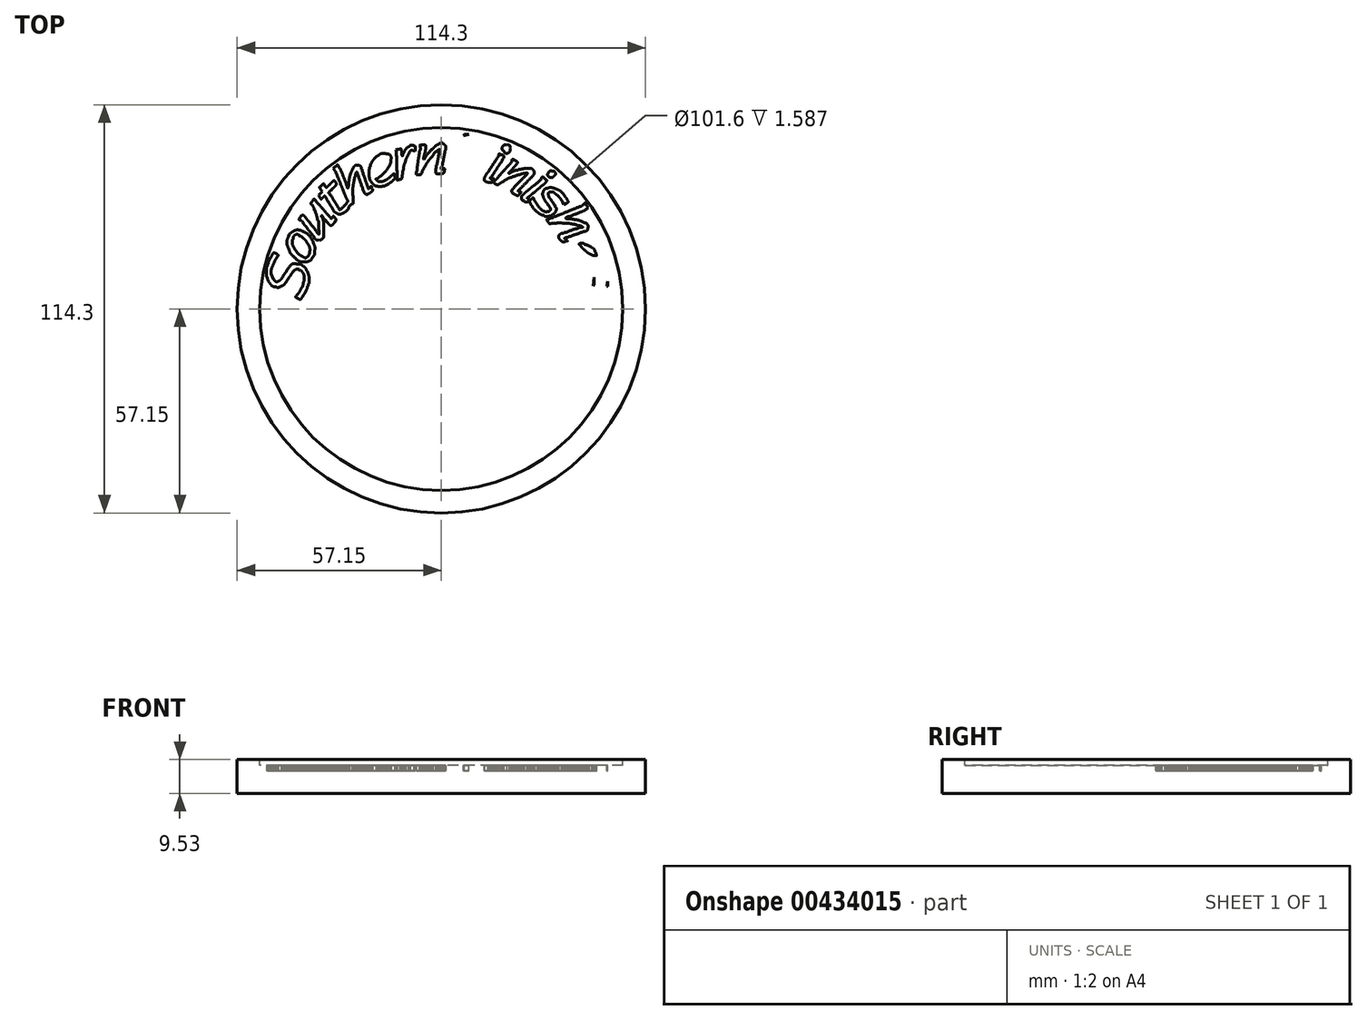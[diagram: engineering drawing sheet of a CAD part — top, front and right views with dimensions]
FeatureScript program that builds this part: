
annotation { "Feature Type Name" : "Feature", "Feature Type Description" : "" }
export const myFeature = defineFeature(function(context is Context, id is Id, definition is map)
    precondition{}
    {
        {
            var Q0;
            Q0=qCreatedBy(makeId("Top.planeOp"),FACE);
            var sketch = newSketch(context, id + "F0", { "sketchPlane" : qUnion([Q0])});
            skCircle(sketch, "E0", {"center": v(0, 0) * mm, "radius": 57.15 * mm});
            skSolve(sketch);
        }
        {
            var Q0;
            Q0 = qSketchRegion(id + "F0", true);
            extrude(context, id + "F1", {"entities" : qUnion([Q0]), "oppositeDirection" : true, "depth" : 9.52 * mm});
        }
        {
            var Q0;
            Q0=qCreatedBy(makeId("Top.planeOp"),FACE);
            var sketch = newSketch(context, id + "F2", { "sketchPlane" : qUnion([Q0])});
            skCircle(sketch, "E1", {"center": v(0, 0) * mm, "radius": 50.8 * mm});
            skSolve(sketch);
        }
        {
            var Q0;
            Q0 = qSketchRegion(id + "F2", true);
            var Q1;
            Q1 = qConstructionFilter(qBodyType(qCreatedBy(id + "F2" ,EDGE), BodyType.WIRE), ConstructionObject.NO);
            extrude(context, id + "F3", {"entities" : qUnion([Q0]), "operationType" : NewBodyOperationType.REMOVE, "surfaceEntities" : qUnion([Q1]), "oppositeDirection" : true, "depth" : 1.59 * mm});
        }
        {
            var Q0;
            Q0=makeQuery(id+"F3.boolean.opBoolean","COPY",FACE,{"derivedFrom":makeQuery(id+"F3.opExtrude","CAP_FACE",FACE,{"disambiguationData":[OSD([sQuery(id+"F2.wireOp",EDGE,"E1")])],"isStart":false})});
            var sketch = newSketch(context, id + "F4", { "sketchPlane" : qUnion([Q0])});
            skFitSpline(sketch, "E2", {"points": [v(-39.96, 2.84) * mm, v(-40.13, 2.95) * mm, v(-40.38, 3.08) * mm, v(-40.51, 3.14) * mm]});
            skFitSpline(sketch, "E3", {"points": [v(-40.51, 3.14) * mm, v(-40.64, 3.2) * mm, v(-40.75, 3.27) * mm, v(-40.75, 3.3) * mm]});
            skFitSpline(sketch, "E4", {"points": [v(-40.75, 3.3) * mm, v(-40.75, 3.4) * mm, v(-40.5, 3.8) * mm, v(-40.3, 4.03) * mm]});
            skFitSpline(sketch, "E5", {"points": [v(-40.3, 4.03) * mm, v(-39.88, 4.52) * mm, v(-39.62, 4.9) * mm, v(-39.38, 5.4) * mm]});
            skFitSpline(sketch, "E6", {"points": [v(-39.38, 5.4) * mm, v(-39.24, 5.7) * mm, v(-39.1, 5.95) * mm, v(-39.06, 5.98) * mm]});
            skFitSpline(sketch, "E7", {"points": [v(-39.06, 5.98) * mm, v(-38.95, 6.08) * mm, v(-38.65, 6.98) * mm, v(-38.65, 7.2) * mm]});
            skFitSpline(sketch, "E8", {"points": [v(-38.65, 7.2) * mm, v(-38.65, 7.33) * mm, v(-38.6, 7.46) * mm, v(-38.56, 7.5) * mm]});
            skFitSpline(sketch, "E9", {"points": [v(-38.56, 7.5) * mm, v(-38.5, 7.52) * mm, v(-38.44, 7.93) * mm, v(-38.4, 8.4) * mm]});
            skFitSpline(sketch, "E10", {"points": [v(-38.4, 8.4) * mm, v(-38.34, 9.07) * mm, v(-38.36, 9.32) * mm, v(-38.5, 9.63) * mm]});
            skFitSpline(sketch, "E11", {"points": [v(-38.5, 9.63) * mm, v(-38.69, 10.05) * mm, v(-39.44, 10.8) * mm, v(-39.67, 10.8) * mm]});
            skFitSpline(sketch, "E12", {"points": [v(-39.67, 10.8) * mm, v(-39.74, 10.8) * mm, v(-39.8, 10.85) * mm, v(-39.8, 10.9) * mm]});
            skFitSpline(sketch, "E13", {"points": [v(-39.8, 10.9) * mm, v(-39.8, 11.08) * mm, v(-40.56, 11.12) * mm, v(-40.89, 10.95) * mm]});
            skFitSpline(sketch, "E14", {"points": [v(-40.89, 10.95) * mm, v(-41.25, 10.76) * mm, v(-41.48, 10.55) * mm, v(-41.48, 10.41) * mm]});
            skFitSpline(sketch, "E15", {"points": [v(-41.48, 10.41) * mm, v(-41.48, 10.36) * mm, v(-41.58, 10.23) * mm, v(-41.7, 10.12) * mm]});
            skFitSpline(sketch, "E16", {"points": [v(-41.7, 10.12) * mm, v(-41.82, 10.01) * mm, v(-41.98, 9.78) * mm, v(-42.07, 9.6) * mm]});
            skFitSpline(sketch, "E17", {"points": [v(-42.07, 9.6) * mm, v(-42.16, 9.41) * mm, v(-42.3, 9.17) * mm, v(-42.4, 9.06) * mm]});
            skFitSpline(sketch, "E18", {"points": [v(-42.4, 9.06) * mm, v(-42.5, 8.95) * mm, v(-42.85, 8.46) * mm, v(-43.18, 7.97) * mm]});
            skFitSpline(sketch, "E19", {"points": [v(-43.18, 7.97) * mm, v(-43.84, 7) * mm, v(-44.17, 6.65) * mm, v(-44.74, 6.38) * mm]});
            skFitSpline(sketch, "E20", {"points": [v(-44.74, 6.38) * mm, v(-45.43, 6.06) * mm, v(-45.87, 5.96) * mm, v(-46.1, 6.08) * mm]});
            skFitSpline(sketch, "E21", {"points": [v(-46.1, 6.08) * mm, v(-46.2, 6.14) * mm, v(-46.4, 6.19) * mm, v(-46.51, 6.19) * mm]});
            skFitSpline(sketch, "E22", {"points": [v(-46.51, 6.19) * mm, v(-46.85, 6.19) * mm, v(-47.56, 6.6) * mm, v(-47.83, 6.96) * mm]});
            skFitSpline(sketch, "E23", {"points": [v(-47.83, 6.96) * mm, v(-48.21, 7.47) * mm, v(-48.62, 8.3) * mm, v(-48.62, 8.56) * mm]});
            skFitSpline(sketch, "E24", {"points": [v(-48.62, 8.56) * mm, v(-48.62, 8.7) * mm, v(-48.67, 8.83) * mm, v(-48.73, 8.87) * mm]});
            skFitSpline(sketch, "E25", {"points": [v(-48.73, 8.87) * mm, v(-48.87, 8.95) * mm, v(-48.87, 11.82) * mm, v(-48.73, 11.9) * mm]});
            skFitSpline(sketch, "E26", {"points": [v(-48.73, 11.9) * mm, v(-48.67, 11.95) * mm, v(-48.62, 12.11) * mm, v(-48.62, 12.28) * mm]});
            skFitSpline(sketch, "E27", {"points": [v(-48.62, 12.28) * mm, v(-48.62, 12.44) * mm, v(-48.57, 12.6) * mm, v(-48.52, 12.64) * mm]});
            skFitSpline(sketch, "E28", {"points": [v(-48.52, 12.64) * mm, v(-48.46, 12.68) * mm, v(-48.41, 12.81) * mm, v(-48.41, 12.94) * mm]});
            skFitSpline(sketch, "E29", {"points": [v(-48.41, 12.94) * mm, v(-48.4, 13.07) * mm, v(-48.35, 13.29) * mm, v(-48.27, 13.43) * mm]});
            skFitSpline(sketch, "E30", {"points": [v(-48.27, 13.43) * mm, v(-48.19, 13.58) * mm, v(-47.98, 13.95) * mm, v(-47.81, 14.27) * mm]});
            skFitSpline(sketch, "E31", {"points": [v(-47.81, 14.27) * mm, v(-47.17, 15.46) * mm, v(-46.95, 15.76) * mm, v(-46.72, 15.69) * mm]});
            skFitSpline(sketch, "E32", {"points": [v(-46.72, 15.69) * mm, v(-46.45, 15.6) * mm, v(-45.68, 15.1) * mm, v(-45.68, 15) * mm]});
            skFitSpline(sketch, "E33", {"points": [v(-45.68, 15) * mm, v(-45.68, 14.96) * mm, v(-45.84, 14.7) * mm, v(-46.02, 14.41) * mm]});
            skFitSpline(sketch, "E34", {"points": [v(-46.02, 14.41) * mm, v(-46.36, 13.91) * mm, v(-46.48, 13.68) * mm, v(-46.94, 12.64) * mm]});
            skFitSpline(sketch, "E35", {"points": [v(-46.94, 12.64) * mm, v(-47.49, 11.43) * mm, v(-47.6, 10.95) * mm, v(-47.61, 9.87) * mm]});
            skFitSpline(sketch, "E36", {"points": [v(-47.05, 8.35) * mm, v(-46.4, 7.7) * mm, v(-46.06, 7.57) * mm, v(-45.55, 7.81) * mm]});
            skFitSpline(sketch, "E37", {"points": [v(-45.55, 7.81) * mm, v(-45.17, 8) * mm, v(-44.56, 8.66) * mm, v(-44.24, 9.25) * mm]});
            skFitSpline(sketch, "E38", {"points": [v(-44.24, 9.25) * mm, v(-44.14, 9.45) * mm, v(-43.9, 9.81) * mm, v(-43.7, 10.04) * mm]});
            skFitSpline(sketch, "E39", {"points": [v(-43.7, 10.04) * mm, v(-43.52, 10.28) * mm, v(-43.37, 10.5) * mm, v(-43.37, 10.54) * mm]});
            skFitSpline(sketch, "E40", {"points": [v(-43.37, 10.54) * mm, v(-43.37, 10.58) * mm, v(-43.22, 10.8) * mm, v(-43.03, 11.05) * mm]});
            skFitSpline(sketch, "E41", {"points": [v(-43.03, 11.05) * mm, v(-42.01, 12.38) * mm, v(-41.55, 12.64) * mm, v(-40.28, 12.57) * mm]});
            skFitSpline(sketch, "E42", {"points": [v(-40.28, 12.57) * mm, v(-39.54, 12.53) * mm, v(-39.36, 12.48) * mm, v(-38.96, 12.2) * mm]});
            skFitSpline(sketch, "E43", {"points": [v(-38.96, 12.2) * mm, v(-38.31, 11.76) * mm, v(-37.94, 11.32) * mm, v(-37.75, 10.78) * mm]});
            skFitSpline(sketch, "E44", {"points": [v(-37.75, 10.78) * mm, v(-37.7, 10.68) * mm, v(-37.65, 10.6) * mm, v(-37.61, 10.6) * mm]});
            skFitSpline(sketch, "E45", {"points": [v(-37.61, 10.6) * mm, v(-37.54, 10.6) * mm, v(-37.39, 10.25) * mm, v(-37.2, 9.65) * mm]});
            skFitSpline(sketch, "E46", {"points": [v(-37.2, 9.65) * mm, v(-37.05, 9.17) * mm, v(-37.03, 7.17) * mm, v(-37.18, 7.08) * mm]});
            skFitSpline(sketch, "E47", {"points": [v(-37.18, 7.08) * mm, v(-37.24, 7.05) * mm, v(-37.28, 6.88) * mm, v(-37.28, 6.71) * mm]});
            skFitSpline(sketch, "E48", {"points": [v(-37.28, 6.71) * mm, v(-37.28, 6.55) * mm, v(-37.33, 6.38) * mm, v(-37.39, 6.35) * mm]});
            skFitSpline(sketch, "E49", {"points": [v(-37.39, 6.35) * mm, v(-37.45, 6.31) * mm, v(-37.5, 6.19) * mm, v(-37.5, 6.08) * mm]});
            skFitSpline(sketch, "E50", {"points": [v(-37.5, 6.08) * mm, v(-37.5, 5.96) * mm, v(-37.54, 5.79) * mm, v(-37.59, 5.69) * mm]});
            skFitSpline(sketch, "E51", {"points": [v(-37.59, 5.69) * mm, v(-37.64, 5.59) * mm, v(-37.77, 5.32) * mm, v(-37.87, 5.09) * mm]});
            skFitSpline(sketch, "E52", {"points": [v(-37.87, 5.09) * mm, v(-37.97, 4.86) * mm, v(-38.17, 4.48) * mm, v(-38.32, 4.24) * mm]});
            skFitSpline(sketch, "E53", {"points": [v(-38.32, 4.24) * mm, v(-38.47, 4.01) * mm, v(-38.64, 3.75) * mm, v(-38.7, 3.66) * mm]});
            skFitSpline(sketch, "E54", {"points": [v(-38.7, 3.66) * mm, v(-39.03, 3.14) * mm, v(-39.45, 2.63) * mm, v(-39.54, 2.63) * mm]});
            skFitSpline(sketch, "E55", {"points": [v(-39.54, 2.63) * mm, v(-39.6, 2.63) * mm, v(-39.79, 2.73) * mm, v(-39.96, 2.84) * mm]});
            skLineSegment(sketch, "E56", {"start": v(-47.05, 8.35) * mm, "end": v(-47.61, 9.87) * mm});
            skFitSpline(sketch, "E57", {"points": [v(40.19, 5.87) * mm, v(40.19, 5.93) * mm, v(40.09, 5.98) * mm, v(39.97, 5.98) * mm]});
            skFitSpline(sketch, "E58", {"points": [v(39.97, 5.98) * mm, v(39.62, 5.98) * mm, v(38.45, 7.18) * mm, v(38.09, 7.9) * mm]});
            skFitSpline(sketch, "E59", {"points": [v(38.09, 7.9) * mm, v(37.91, 8.25) * mm, v(37.77, 8.62) * mm, v(37.77, 8.72) * mm]});
            skFitSpline(sketch, "E60", {"points": [v(37.77, 8.72) * mm, v(37.77, 8.83) * mm, v(37.73, 8.92) * mm, v(37.68, 8.92) * mm]});
            skFitSpline(sketch, "E61", {"points": [v(37.68, 8.92) * mm, v(37.46, 8.92) * mm, v(37.27, 11.76) * mm, v(37.46, 12.12) * mm]});
            skFitSpline(sketch, "E62", {"points": [v(37.46, 12.12) * mm, v(37.57, 12.33) * mm, v(37.53, 12.4) * mm, v(37.05, 12.87) * mm]});
            skFitSpline(sketch, "E63", {"points": [v(37.05, 12.87) * mm, v(36.47, 13.43) * mm, v(36.1, 13.91) * mm, v(35.82, 14.48) * mm]});
            skFitSpline(sketch, "E64", {"points": [v(35.82, 14.48) * mm, v(35.71, 14.68) * mm, v(35.6, 14.87) * mm, v(35.57, 14.9) * mm]});
            skFitSpline(sketch, "E65", {"points": [v(35.57, 14.9) * mm, v(35.2, 15.2) * mm, v(35.06, 17.2) * mm, v(35.35, 17.8) * mm]});
            skFitSpline(sketch, "E66", {"points": [v(35.35, 17.8) * mm, v(35.54, 18.18) * mm, v(36.18, 18.88) * mm, v(36.46, 19) * mm]});
            skFitSpline(sketch, "E67", {"points": [v(36.46, 19) * mm, v(36.58, 19.06) * mm, v(36.74, 19.14) * mm, v(36.83, 19.19) * mm]});
            skFitSpline(sketch, "E68", {"points": [v(36.83, 19.19) * mm, v(37.29, 19.45) * mm, v(37.48, 19.52) * mm, v(37.71, 19.52) * mm]});
            skFitSpline(sketch, "E69", {"points": [v(37.71, 19.52) * mm, v(37.85, 19.52) * mm, v(38, 19.57) * mm, v(38.03, 19.63) * mm]});
            skFitSpline(sketch, "E70", {"points": [v(38.03, 19.63) * mm, v(38.07, 19.68) * mm, v(38.5, 19.73) * mm, v(38.98, 19.73) * mm]});
            skFitSpline(sketch, "E71", {"points": [v(38.98, 19.73) * mm, v(39.46, 19.73) * mm, v(39.89, 19.68) * mm, v(39.92, 19.63) * mm]});
            skFitSpline(sketch, "E72", {"points": [v(39.92, 19.63) * mm, v(39.96, 19.57) * mm, v(40.13, 19.52) * mm, v(40.3, 19.52) * mm]});
            skFitSpline(sketch, "E73", {"points": [v(40.3, 19.52) * mm, v(40.47, 19.52) * mm, v(40.7, 19.48) * mm, v(40.8, 19.43) * mm]});
            skFitSpline(sketch, "E74", {"points": [v(40.8, 19.43) * mm, v(40.9, 19.37) * mm, v(41.19, 19.25) * mm, v(41.45, 19.14) * mm]});
            skFitSpline(sketch, "E75", {"points": [v(41.45, 19.14) * mm, v(42.11, 18.87) * mm, v(43.3, 18.1) * mm, v(43.52, 17.78) * mm]});
            skFitSpline(sketch, "E76", {"points": [v(43.52, 17.78) * mm, v(43.62, 17.63) * mm, v(43.8, 17.4) * mm, v(43.91, 17.28) * mm]});
            skFitSpline(sketch, "E77", {"points": [v(43.91, 17.28) * mm, v(44.14, 17.04) * mm, v(44.32, 16.69) * mm, v(44.45, 16.27) * mm]});
            skFitSpline(sketch, "E78", {"points": [v(44.45, 16.27) * mm, v(44.59, 15.84) * mm, v(44.57, 14.88) * mm, v(44.42, 14.59) * mm]});
            skFitSpline(sketch, "E79", {"points": [v(44.42, 14.59) * mm, v(44.28, 14.3) * mm, v(43.84, 13.88) * mm, v(43.47, 13.67) * mm]});
            skFitSpline(sketch, "E80", {"points": [v(43.47, 13.67) * mm, v(43.19, 13.51) * mm, v(42.22, 13.5) * mm, v(42.13, 13.64) * mm]});
            skFitSpline(sketch, "E81", {"points": [v(42.13, 13.64) * mm, v(42.1, 13.7) * mm, v(41.95, 13.75) * mm, v(41.8, 13.75) * mm]});
            skFitSpline(sketch, "E82", {"points": [v(41.8, 13.75) * mm, v(41.67, 13.75) * mm, v(41.55, 13.8) * mm, v(41.55, 13.85) * mm]});
            skFitSpline(sketch, "E83", {"points": [v(41.55, 13.85) * mm, v(41.55, 13.9) * mm, v(41.48, 13.96) * mm, v(41.38, 13.96) * mm]});
            skFitSpline(sketch, "E84", {"points": [v(41.38, 13.96) * mm, v(41.3, 13.96) * mm, v(41.1, 14.04) * mm, v(40.94, 14.14) * mm]});
            skFitSpline(sketch, "E85", {"points": [v(40.94, 14.14) * mm, v(40.44, 14.47) * mm, v(40.24, 14.59) * mm, v(40.03, 14.68) * mm]});
            skFitSpline(sketch, "E86", {"points": [v(40.03, 14.68) * mm, v(39.8, 14.79) * mm, v(37.73, 16.9) * mm, v(37.42, 17.34) * mm]});
            skFitSpline(sketch, "E87", {"points": [v(37.42, 17.34) * mm, v(37.16, 17.72) * mm, v(36.99, 17.7) * mm, v(36.78, 17.3) * mm]});
            skFitSpline(sketch, "E88", {"points": [v(36.78, 17.3) * mm, v(36.52, 16.78) * mm, v(36.57, 15.93) * mm, v(36.9, 15.3) * mm]});
            skFitSpline(sketch, "E89", {"points": [v(36.9, 15.3) * mm, v(37.05, 15) * mm, v(37.21, 14.73) * mm, v(37.26, 14.7) * mm]});
            skFitSpline(sketch, "E90", {"points": [v(37.26, 14.7) * mm, v(37.31, 14.69) * mm, v(37.35, 14.62) * mm, v(37.35, 14.55) * mm]});
            skFitSpline(sketch, "E91", {"points": [v(37.35, 14.55) * mm, v(37.35, 14.48) * mm, v(37.57, 14.2) * mm, v(37.83, 13.93) * mm]});
            skFitSpline(sketch, "E92", {"points": [v(37.83, 13.93) * mm, v(38.08, 13.66) * mm, v(38.3, 13.4) * mm, v(38.3, 13.35) * mm]});
            skFitSpline(sketch, "E93", {"points": [v(38.3, 13.35) * mm, v(38.3, 13.3) * mm, v(38.42, 13.18) * mm, v(38.56, 13.07) * mm]});
            skFitSpline(sketch, "E94", {"points": [v(38.56, 13.07) * mm, v(38.82, 12.88) * mm, v(38.82, 12.87) * mm, v(38.82, 11.11) * mm]});
            skFitSpline(sketch, "E95", {"points": [v(38.82, 11.11) * mm, v(38.82, 10.05) * mm, v(38.86, 9.32) * mm, v(38.93, 9.29) * mm]});
            skFitSpline(sketch, "E96", {"points": [v(38.93, 9.29) * mm, v(38.98, 9.25) * mm, v(39.03, 9.14) * mm, v(39.03, 9.04) * mm]});
            skFitSpline(sketch, "E97", {"points": [v(39.03, 9.04) * mm, v(39.03, 8.94) * mm, v(39.13, 8.74) * mm, v(39.26, 8.6) * mm]});
            skFitSpline(sketch, "E98", {"points": [v(39.26, 8.6) * mm, v(39.38, 8.47) * mm, v(39.49, 8.23) * mm, v(39.49, 8.06) * mm]});
            skFitSpline(sketch, "E99", {"points": [v(39.49, 8.06) * mm, v(39.49, 7.87) * mm, v(39.54, 7.76) * mm, v(39.64, 7.76) * mm]});
            skFitSpline(sketch, "E100", {"points": [v(39.64, 7.76) * mm, v(39.72, 7.76) * mm, v(39.77, 7.7) * mm, v(39.73, 7.62) * mm]});
            skFitSpline(sketch, "E101", {"points": [v(39.73, 7.62) * mm, v(39.61, 7.3) * mm, v(40.7, 7.03) * mm, v(41.08, 7.28) * mm]});
            skFitSpline(sketch, "E102", {"points": [v(41.08, 7.28) * mm, v(41.34, 7.45) * mm, v(41.34, 7.46) * mm, v(41.34, 9.28) * mm]});
            skFitSpline(sketch, "E103", {"points": [v(41.34, 9.28) * mm, v(41.34, 10.41) * mm, v(41.39, 11.23) * mm, v(41.46, 11.4) * mm]});
            skFitSpline(sketch, "E104", {"points": [v(41.46, 11.4) * mm, v(41.8, 12.23) * mm, v(41.9, 12.38) * mm, v(42.24, 12.58) * mm]});
            skFitSpline(sketch, "E105", {"points": [v(42.24, 12.58) * mm, v(42.7, 12.85) * mm, v(43.65, 12.88) * mm, v(44.24, 12.64) * mm]});
            skFitSpline(sketch, "E106", {"points": [v(44.24, 12.64) * mm, v(44.75, 12.43) * mm, v(45.73, 11.43) * mm, v(46.03, 10.8) * mm]});
            skFitSpline(sketch, "E107", {"points": [v(46.03, 10.8) * mm, v(46.28, 10.29) * mm, v(46.5, 9.62) * mm, v(46.47, 9.48) * mm]});
            skFitSpline(sketch, "E108", {"points": [v(46.47, 9.48) * mm, v(46.46, 9.43) * mm, v(46.48, 9.32) * mm, v(46.52, 9.23) * mm]});
            skFitSpline(sketch, "E109", {"points": [v(46.52, 9.23) * mm, v(46.56, 9.14) * mm, v(46.58, 8.45) * mm, v(46.57, 7.7) * mm]});
            skFitSpline(sketch, "E110", {"points": [v(46.28, 6.38) * mm, v(44.99, 6.54) * mm, v(45.1, 6.5) * mm, v(45.18, 6.86) * mm]});
            skFitSpline(sketch, "E111", {"points": [v(45.18, 6.86) * mm, v(45.32, 7.5) * mm, v(45.23, 9.2) * mm, v(45.02, 9.7) * mm]});
            skFitSpline(sketch, "E112", {"points": [v(45.02, 9.7) * mm, v(44.97, 9.82) * mm, v(44.85, 10.2) * mm, v(44.74, 10.53) * mm]});
            skFitSpline(sketch, "E113", {"points": [v(44.74, 10.53) * mm, v(44.56, 11.1) * mm, v(44.5, 11.17) * mm, v(44.08, 11.35) * mm]});
            skFitSpline(sketch, "E114", {"points": [v(44.08, 11.35) * mm, v(43.7, 11.52) * mm, v(43.58, 11.53) * mm, v(43.33, 11.42) * mm]});
            skFitSpline(sketch, "E115", {"points": [v(43.33, 11.42) * mm, v(43.17, 11.35) * mm, v(43, 11.2) * mm, v(42.96, 11.07) * mm]});
            skFitSpline(sketch, "E116", {"points": [v(42.96, 11.07) * mm, v(42.91, 10.96) * mm, v(42.85, 9.93) * mm, v(42.82, 8.8) * mm]});
            skLineSegment(sketch, "E117", {"start": v(46.57, 7.7) * mm, "end": v(46.54, 6.35) * mm});
            skLineSegment(sketch, "E118", {"start": v(46.54, 6.35) * mm, "end": v(46.28, 6.38) * mm});
            skLineSegment(sketch, "E119", {"start": v(46.28, 6.38) * mm, "end": v(46.57, 7.7) * mm});
            skFitSpline(sketch, "E120", {"points": [v(42.45, 6.4) * mm, v(42.27, 6.22) * mm, v(42, 6) * mm, v(41.83, 5.92) * mm]});
            skFitSpline(sketch, "E121", {"points": [v(41.83, 5.92) * mm, v(41.48, 5.75) * mm, v(40.19, 5.71) * mm, v(40.19, 5.87) * mm]});
            skLineSegment(sketch, "E122", {"start": v(42.82, 8.8) * mm, "end": v(42.76, 6.73) * mm});
            skLineSegment(sketch, "E123", {"start": v(42.76, 6.73) * mm, "end": v(42.45, 6.4) * mm});
            skLineSegment(sketch, "E124", {"start": v(42.45, 6.4) * mm, "end": v(42.82, 8.8) * mm});
            skFitSpline(sketch, "E125", {"points": [v(43.4, 15.14) * mm, v(43.35, 15.27) * mm, v(43.3, 15.48) * mm, v(43.26, 15.61) * mm]});
            skFitSpline(sketch, "E126", {"points": [v(43.26, 15.61) * mm, v(43.23, 15.74) * mm, v(43.17, 15.85) * mm, v(43.13, 15.85) * mm]});
            skFitSpline(sketch, "E127", {"points": [v(43.13, 15.85) * mm, v(43.08, 15.85) * mm, v(43.01, 15.97) * mm, v(42.98, 16.11) * mm]});
            skFitSpline(sketch, "E128", {"points": [v(42.98, 16.11) * mm, v(42.87, 16.53) * mm, v(42.23, 17.17) * mm, v(41.55, 17.52) * mm]});
            skFitSpline(sketch, "E129", {"points": [v(41.55, 17.52) * mm, v(41.2, 17.7) * mm, v(40.86, 17.84) * mm, v(40.77, 17.84) * mm]});
            skFitSpline(sketch, "E130", {"points": [v(40.77, 17.84) * mm, v(40.68, 17.84) * mm, v(40.6, 17.89) * mm, v(40.6, 17.95) * mm]});
            skFitSpline(sketch, "E131", {"points": [v(40.6, 17.95) * mm, v(40.6, 18) * mm, v(40.46, 18.05) * mm, v(40.3, 18.05) * mm]});
            skFitSpline(sketch, "E132", {"points": [v(40.3, 18.05) * mm, v(40.12, 18.05) * mm, v(39.98, 18.1) * mm, v(39.98, 18.16) * mm]});
            skFitSpline(sketch, "E133", {"points": [v(39.98, 18.16) * mm, v(39.98, 18.27) * mm, v(38.7, 18.3) * mm, v(38.58, 18.2) * mm]});
            skFitSpline(sketch, "E134", {"points": [v(38.58, 18.2) * mm, v(38.54, 18.15) * mm, v(38.7, 17.93) * mm, v(38.91, 17.69) * mm]});
            skFitSpline(sketch, "E135", {"points": [v(38.91, 17.69) * mm, v(39.13, 17.45) * mm, v(39.36, 17.18) * mm, v(39.4, 17.1) * mm]});
            skFitSpline(sketch, "E136", {"points": [v(39.4, 17.1) * mm, v(39.46, 17.01) * mm, v(39.74, 16.75) * mm, v(40.03, 16.52) * mm]});
            skFitSpline(sketch, "E137", {"points": [v(40.03, 16.52) * mm, v(40.32, 16.3) * mm, v(40.58, 16.07) * mm, v(40.61, 16.03) * mm]});
            skFitSpline(sketch, "E138", {"points": [v(40.61, 16.03) * mm, v(40.68, 15.94) * mm, v(41.68, 15.34) * mm, v(42.08, 15.14) * mm]});
            skFitSpline(sketch, "E139", {"points": [v(42.08, 15.14) * mm, v(42.4, 14.99) * mm, v(42.66, 14.93) * mm, v(43.11, 14.91) * mm]});
            skFitSpline(sketch, "E140", {"points": [v(43.11, 14.91) * mm, v(43.43, 14.9) * mm, v(43.46, 14.92) * mm, v(43.4, 15.14) * mm]});
            skFitSpline(sketch, "E141", {"points": [v(-38.75, 13.2) * mm, v(-39.48, 13.24) * mm, v(-40.4, 13.75) * mm, v(-41.22, 14.56) * mm]});
            skFitSpline(sketch, "E142", {"points": [v(-41.22, 14.56) * mm, v(-42.1, 15.42) * mm, v(-42.33, 15.73) * mm, v(-42.57, 16.42) * mm]});
            skFitSpline(sketch, "E143", {"points": [v(-42.57, 16.42) * mm, v(-42.67, 16.71) * mm, v(-42.8, 17.04) * mm, v(-42.85, 17.16) * mm]});
            skFitSpline(sketch, "E144", {"points": [v(-42.85, 17.16) * mm, v(-43.18, 17.92) * mm, v(-43.15, 19.4) * mm, v(-42.78, 20.22) * mm]});
            skFitSpline(sketch, "E145", {"points": [v(-42.78, 20.22) * mm, v(-42.7, 20.4) * mm, v(-42.64, 20.59) * mm, v(-42.64, 20.63) * mm]});
            skFitSpline(sketch, "E146", {"points": [v(-42.64, 20.63) * mm, v(-42.64, 20.79) * mm, v(-41.7, 21.6) * mm, v(-41.3, 21.8) * mm]});
            skFitSpline(sketch, "E147", {"points": [v(-41.3, 21.8) * mm, v(-40.69, 22.09) * mm, v(-39.49, 22.04) * mm, v(-38.75, 21.7) * mm]});
            skFitSpline(sketch, "E148", {"points": [v(-38.75, 21.7) * mm, v(-37.63, 21.16) * mm, v(-36.76, 20.32) * mm, v(-36.07, 19.11) * mm]});
            skFitSpline(sketch, "E149", {"points": [v(-36.07, 19.11) * mm, v(-35.93, 18.86) * mm, v(-35.81, 18.59) * mm, v(-35.81, 18.5) * mm]});
            skFitSpline(sketch, "E150", {"points": [v(-35.81, 18.5) * mm, v(-35.81, 18.43) * mm, v(-35.77, 18.28) * mm, v(-35.72, 18.18) * mm]});
            skFitSpline(sketch, "E151", {"points": [v(-35.72, 18.18) * mm, v(-35.48, 17.72) * mm, v(-35.38, 17.1) * mm, v(-35.42, 16.37) * mm]});
            skFitSpline(sketch, "E152", {"points": [v(-35.42, 16.37) * mm, v(-35.49, 15.34) * mm, v(-35.57, 15.03) * mm, v(-35.9, 14.59) * mm]});
            skFitSpline(sketch, "E153", {"points": [v(-35.9, 14.59) * mm, v(-36.06, 14.39) * mm, v(-36.23, 14.13) * mm, v(-36.29, 14.03) * mm]});
            skFitSpline(sketch, "E154", {"points": [v(-36.29, 14.03) * mm, v(-36.44, 13.75) * mm, v(-37.39, 13.25) * mm, v(-37.87, 13.2) * mm]});
            skFitSpline(sketch, "E155", {"points": [v(-37.87, 13.2) * mm, v(-38.1, 13.19) * mm, v(-38.5, 13.18) * mm, v(-38.75, 13.2) * mm]});
            skFitSpline(sketch, "E156", {"points": [v(-37.78, 14.4) * mm, v(-37.65, 14.46) * mm, v(-37.5, 14.57) * mm, v(-37.44, 14.63) * mm]});
            skFitSpline(sketch, "E157", {"points": [v(-37.44, 14.63) * mm, v(-37.22, 14.85) * mm, v(-36.87, 15.7) * mm, v(-36.83, 16.12) * mm]});
            skFitSpline(sketch, "E158", {"points": [v(-36.83, 16.12) * mm, v(-36.77, 16.6) * mm, v(-37.02, 17.66) * mm, v(-37.27, 18.05) * mm]});
            skFitSpline(sketch, "E159", {"points": [v(-37.27, 18.05) * mm, v(-37.36, 18.2) * mm, v(-37.49, 18.39) * mm, v(-37.55, 18.48) * mm]});
            skFitSpline(sketch, "E160", {"points": [v(-37.55, 18.48) * mm, v(-37.89, 19.03) * mm, v(-38.09, 19.3) * mm, v(-38.38, 19.56) * mm]});
            skFitSpline(sketch, "E161", {"points": [v(-38.38, 19.56) * mm, v(-38.8, 19.95) * mm, v(-39.55, 20.47) * mm, v(-39.7, 20.47) * mm]});
            skFitSpline(sketch, "E162", {"points": [v(-39.7, 20.47) * mm, v(-39.75, 20.47) * mm, v(-39.8, 20.5) * mm, v(-39.8, 20.54) * mm]});
            skFitSpline(sketch, "E163", {"points": [v(-39.8, 20.54) * mm, v(-39.8, 20.7) * mm, v(-40.56, 20.87) * mm, v(-40.8, 20.76) * mm]});
            skFitSpline(sketch, "E164", {"points": [v(-40.8, 20.76) * mm, v(-41.06, 20.64) * mm, v(-41.48, 20) * mm, v(-41.48, 19.73) * mm]});
            skFitSpline(sketch, "E165", {"points": [v(-41.48, 19.73) * mm, v(-41.48, 19.62) * mm, v(-41.53, 19.5) * mm, v(-41.59, 19.47) * mm]});
            skFitSpline(sketch, "E166", {"points": [v(-41.59, 19.47) * mm, v(-41.65, 19.43) * mm, v(-41.7, 19.18) * mm, v(-41.7, 18.92) * mm]});
            skFitSpline(sketch, "E167", {"points": [v(-41.7, 18.92) * mm, v(-41.7, 18.27) * mm, v(-41.47, 17.6) * mm, v(-40.96, 16.7) * mm]});
            skFitSpline(sketch, "E168", {"points": [v(-40.96, 16.7) * mm, v(-40.72, 16.27) * mm, v(-39.53, 15.04) * mm, v(-39.23, 14.89) * mm]});
            skFitSpline(sketch, "E169", {"points": [v(-39.23, 14.89) * mm, v(-39.11, 14.83) * mm, v(-38.83, 14.67) * mm, v(-38.6, 14.54) * mm]});
            skFitSpline(sketch, "E170", {"points": [v(-38.6, 14.54) * mm, v(-38.1, 14.24) * mm, v(-38.07, 14.24) * mm, v(-37.78, 14.4) * mm]});
            skFitSpline(sketch, "E171", {"points": [v(33.58, 19.06) * mm, v(33.14, 19.45) * mm, v(32.84, 19.94) * mm, v(32.84, 20.27) * mm]});
            skFitSpline(sketch, "E172", {"points": [v(32.84, 20.27) * mm, v(32.84, 20.5) * mm, v(33.75, 21.2) * mm, v(34.07, 21.2) * mm]});
            skFitSpline(sketch, "E173", {"points": [v(34.07, 21.2) * mm, v(34.2, 21.2) * mm, v(34.32, 21.25) * mm, v(34.36, 21.3) * mm]});
            skFitSpline(sketch, "E174", {"points": [v(34.36, 21.3) * mm, v(34.4, 21.36) * mm, v(34.52, 21.4) * mm, v(34.64, 21.4) * mm]});
            skFitSpline(sketch, "E175", {"points": [v(34.64, 21.4) * mm, v(34.84, 21.4) * mm, v(35.35, 21.6) * mm, v(35.8, 21.84) * mm]});
            skFitSpline(sketch, "E176", {"points": [v(35.8, 21.84) * mm, v(35.9, 21.9) * mm, v(36.06, 21.93) * mm, v(36.15, 21.93) * mm]});
            skFitSpline(sketch, "E177", {"points": [v(36.15, 21.93) * mm, v(36.23, 21.93) * mm, v(36.4, 21.98) * mm, v(36.51, 22.04) * mm]});
            skFitSpline(sketch, "E178", {"points": [v(36.51, 22.04) * mm, v(36.63, 22.1) * mm, v(36.8, 22.19) * mm, v(36.91, 22.24) * mm]});
            skFitSpline(sketch, "E179", {"points": [v(36.91, 22.24) * mm, v(37.01, 22.29) * mm, v(37.3, 22.36) * mm, v(37.56, 22.4) * mm]});
            skFitSpline(sketch, "E180", {"points": [v(37.56, 22.4) * mm, v(37.82, 22.45) * mm, v(38.12, 22.53) * mm, v(38.24, 22.6) * mm]});
            skFitSpline(sketch, "E181", {"points": [v(38.24, 22.6) * mm, v(38.74, 22.85) * mm, v(38.83, 22.88) * mm, v(39.03, 22.88) * mm]});
            skFitSpline(sketch, "E182", {"points": [v(39.03, 22.88) * mm, v(39.62, 22.88) * mm, v(38.99, 23.27) * mm, v(38.23, 23.37) * mm]});
            skFitSpline(sketch, "E183", {"points": [v(38.23, 23.37) * mm, v(37.98, 23.4) * mm, v(37.77, 23.47) * mm, v(37.77, 23.51) * mm]});
            skFitSpline(sketch, "E184", {"points": [v(37.77, 23.51) * mm, v(37.77, 23.56) * mm, v(37.57, 23.62) * mm, v(37.33, 23.66) * mm]});
            skFitSpline(sketch, "E185", {"points": [v(37.33, 23.66) * mm, v(37.08, 23.7) * mm, v(36.57, 23.78) * mm, v(36.2, 23.84) * mm]});
            skFitSpline(sketch, "E186", {"points": [v(36.2, 23.84) * mm, v(35.47, 23.96) * mm, v(31.39, 24) * mm, v(30.69, 23.9) * mm]});
            skFitSpline(sketch, "E187", {"points": [v(30.69, 23.9) * mm, v(30.28, 23.83) * mm, v(30.25, 23.84) * mm, v(29.92, 24.3) * mm]});
            skFitSpline(sketch, "E188", {"points": [v(29.92, 24.3) * mm, v(29.57, 24.79) * mm, v(29.54, 25.08) * mm, v(29.84, 25.08) * mm]});
            skFitSpline(sketch, "E189", {"points": [v(29.84, 25.08) * mm, v(29.93, 25.08) * mm, v(30.15, 25.17) * mm, v(30.34, 25.28) * mm]});
            skFitSpline(sketch, "E190", {"points": [v(30.34, 25.28) * mm, v(30.53, 25.38) * mm, v(30.86, 25.5) * mm, v(31.08, 25.54) * mm]});
            skFitSpline(sketch, "E191", {"points": [v(31.08, 25.54) * mm, v(31.3, 25.59) * mm, v(31.47, 25.66) * mm, v(31.47, 25.72) * mm]});
            skFitSpline(sketch, "E192", {"points": [v(31.47, 25.72) * mm, v(31.47, 25.77) * mm, v(31.55, 25.82) * mm, v(31.63, 25.82) * mm]});
            skFitSpline(sketch, "E193", {"points": [v(31.63, 25.82) * mm, v(31.72, 25.82) * mm, v(32, 25.9) * mm, v(32.24, 26.01) * mm]});
            skFitSpline(sketch, "E194", {"points": [v(32.24, 26.01) * mm, v(32.48, 26.12) * mm, v(32.9, 26.3) * mm, v(33.15, 26.4) * mm]});
            skFitSpline(sketch, "E195", {"points": [v(33.15, 26.4) * mm, v(33.41, 26.5) * mm, v(33.72, 26.62) * mm, v(33.84, 26.66) * mm]});
            skFitSpline(sketch, "E196", {"points": [v(33.84, 26.66) * mm, v(33.95, 26.7) * mm, v(34.27, 26.84) * mm, v(34.54, 26.96) * mm]});
            skFitSpline(sketch, "E197", {"points": [v(34.54, 26.96) * mm, v(34.82, 27.08) * mm, v(35.07, 27.18) * mm, v(35.1, 27.18) * mm]});
            skFitSpline(sketch, "E198", {"points": [v(35.1, 27.18) * mm, v(35.14, 27.18) * mm, v(35.34, 27.26) * mm, v(35.55, 27.35) * mm]});
            skFitSpline(sketch, "E199", {"points": [v(35.55, 27.35) * mm, v(35.76, 27.44) * mm, v(36.03, 27.56) * mm, v(36.15, 27.6) * mm]});
            skFitSpline(sketch, "E200", {"points": [v(36.15, 27.6) * mm, v(36.26, 27.65) * mm, v(36.53, 27.76) * mm, v(36.74, 27.86) * mm]});
            skFitSpline(sketch, "E201", {"points": [v(36.74, 27.86) * mm, v(36.95, 27.95) * mm, v(37.17, 28.02) * mm, v(37.23, 28.02) * mm]});
            skFitSpline(sketch, "E202", {"points": [v(37.23, 28.02) * mm, v(37.3, 28.02) * mm, v(37.51, 28.12) * mm, v(37.72, 28.23) * mm]});
            skFitSpline(sketch, "E203", {"points": [v(37.72, 28.23) * mm, v(37.93, 28.35) * mm, v(38.19, 28.44) * mm, v(38.3, 28.44) * mm]});
            skFitSpline(sketch, "E204", {"points": [v(38.3, 28.44) * mm, v(38.41, 28.44) * mm, v(38.5, 28.5) * mm, v(38.5, 28.55) * mm]});
            skFitSpline(sketch, "E205", {"points": [v(38.5, 28.55) * mm, v(38.5, 28.6) * mm, v(38.58, 28.65) * mm, v(38.67, 28.65) * mm]});
            skFitSpline(sketch, "E206", {"points": [v(38.67, 28.65) * mm, v(38.92, 28.65) * mm, v(39.47, 28.96) * mm, v(39.84, 29.3) * mm]});
            skFitSpline(sketch, "E207", {"points": [v(39.84, 29.3) * mm, v(40.16, 29.61) * mm, v(40.4, 29.63) * mm, v(40.4, 29.34) * mm]});
            skFitSpline(sketch, "E208", {"points": [v(40.4, 29.34) * mm, v(40.4, 29.26) * mm, v(40.43, 29.18) * mm, v(40.48, 29.16) * mm]});
            skFitSpline(sketch, "E209", {"points": [v(40.48, 29.16) * mm, v(40.52, 29.14) * mm, v(40.7, 28.94) * mm, v(40.86, 28.72) * mm]});
            skFitSpline(sketch, "E210", {"points": [v(40.91, 28.12) * mm, v(40.77, 28.01) * mm, v(40.6, 27.92) * mm, v(40.53, 27.92) * mm]});
            skFitSpline(sketch, "E211", {"points": [v(40.53, 27.92) * mm, v(40.46, 27.92) * mm, v(40.4, 27.88) * mm, v(40.4, 27.84) * mm]});
            skFitSpline(sketch, "E212", {"points": [v(40.4, 27.84) * mm, v(40.4, 27.77) * mm, v(39.37, 27.25) * mm, v(38.87, 27.08) * mm]});
            skFitSpline(sketch, "E213", {"points": [v(38.87, 27.08) * mm, v(38.76, 27.03) * mm, v(38.45, 26.9) * mm, v(38.2, 26.78) * mm]});
            skFitSpline(sketch, "E214", {"points": [v(38.2, 26.78) * mm, v(37.93, 26.66) * mm, v(37.6, 26.54) * mm, v(37.46, 26.5) * mm]});
            skFitSpline(sketch, "E215", {"points": [v(37.46, 26.5) * mm, v(37.2, 26.43) * mm, v(36.74, 26.24) * mm, v(36.16, 25.96) * mm]});
            skFitSpline(sketch, "E216", {"points": [v(36.16, 25.96) * mm, v(35.99, 25.88) * mm, v(35.78, 25.82) * mm, v(35.7, 25.82) * mm]});
            skFitSpline(sketch, "E217", {"points": [v(35.7, 25.82) * mm, v(35.48, 25.82) * mm, v(34.83, 25.5) * mm, v(34.83, 25.39) * mm]});
            skFitSpline(sketch, "E218", {"points": [v(34.83, 25.39) * mm, v(34.83, 25.34) * mm, v(35.2, 25.3) * mm, v(35.65, 25.3) * mm]});
            skFitSpline(sketch, "E219", {"points": [v(35.65, 25.3) * mm, v(36.1, 25.3) * mm, v(36.52, 25.25) * mm, v(36.57, 25.2) * mm]});
            skFitSpline(sketch, "E220", {"points": [v(36.57, 25.2) * mm, v(36.63, 25.15) * mm, v(36.88, 25.08) * mm, v(37.14, 25.05) * mm]});
            skFitSpline(sketch, "E221", {"points": [v(37.14, 25.05) * mm, v(37.69, 25) * mm, v(38.57, 24.8) * mm, v(38.87, 24.67) * mm]});
            skFitSpline(sketch, "E222", {"points": [v(38.87, 24.67) * mm, v(39, 24.62) * mm, v(39.35, 24.46) * mm, v(39.67, 24.3) * mm]});
            skFitSpline(sketch, "E223", {"points": [v(39.67, 24.3) * mm, v(40, 24.16) * mm, v(40.31, 24.03) * mm, v(40.37, 24.03) * mm]});
            skFitSpline(sketch, "E224", {"points": [v(40.37, 24.03) * mm, v(40.54, 24.03) * mm, v(41.02, 23.43) * mm, v(41.1, 23.13) * mm]});
            skFitSpline(sketch, "E225", {"points": [v(41.1, 23.13) * mm, v(41.13, 22.98) * mm, v(41.1, 22.81) * mm, v(41.04, 22.75) * mm]});
            skFitSpline(sketch, "E226", {"points": [v(41.04, 22.75) * mm, v(40.97, 22.68) * mm, v(40.92, 22.54) * mm, v(40.92, 22.43) * mm]});
            skFitSpline(sketch, "E227", {"points": [v(40.92, 22.43) * mm, v(40.92, 22.14) * mm, v(40.43, 21.75) * mm, v(39.97, 21.67) * mm]});
            skFitSpline(sketch, "E228", {"points": [v(39.97, 21.67) * mm, v(39.74, 21.63) * mm, v(39.53, 21.56) * mm, v(39.5, 21.5) * mm]});
            skFitSpline(sketch, "E229", {"points": [v(39.5, 21.5) * mm, v(39.47, 21.45) * mm, v(39.35, 21.4) * mm, v(39.23, 21.4) * mm]});
            skFitSpline(sketch, "E230", {"points": [v(39.23, 21.4) * mm, v(39.12, 21.4) * mm, v(38.95, 21.37) * mm, v(38.85, 21.32) * mm]});
            skFitSpline(sketch, "E231", {"points": [v(38.85, 21.32) * mm, v(38.51, 21.15) * mm, v(38.15, 21.01) * mm, v(37.56, 20.84) * mm]});
            skFitSpline(sketch, "E232", {"points": [v(37.56, 20.84) * mm, v(37, 20.67) * mm, v(36.65, 20.54) * mm, v(36.28, 20.35) * mm]});
            skFitSpline(sketch, "E233", {"points": [v(36.28, 20.35) * mm, v(36.18, 20.3) * mm, v(36, 20.26) * mm, v(35.9, 20.26) * mm]});
            skFitSpline(sketch, "E234", {"points": [v(35.9, 20.26) * mm, v(35.78, 20.26) * mm, v(35.66, 20.21) * mm, v(35.63, 20.16) * mm]});
            skFitSpline(sketch, "E235", {"points": [v(35.63, 20.16) * mm, v(35.6, 20.11) * mm, v(35.36, 20.04) * mm, v(35.1, 20) * mm]});
            skFitSpline(sketch, "E236", {"points": [v(35.1, 20) * mm, v(34.84, 19.96) * mm, v(34.6, 19.88) * mm, v(34.56, 19.82) * mm]});
            skFitSpline(sketch, "E237", {"points": [v(34.56, 19.82) * mm, v(34.53, 19.76) * mm, v(34.68, 19.56) * mm, v(34.9, 19.36) * mm]});
            skFitSpline(sketch, "E238", {"points": [v(34.9, 19.36) * mm, v(35.3, 19) * mm, v(35.3, 19) * mm, v(35.03, 19) * mm]});
            skFitSpline(sketch, "E239", {"points": [v(35.03, 19) * mm, v(34.87, 19) * mm, v(34.73, 18.96) * mm, v(34.71, 18.9) * mm]});
            skFitSpline(sketch, "E240", {"points": [v(34.71, 18.9) * mm, v(34.7, 18.86) * mm, v(34.53, 18.79) * mm, v(34.34, 18.75) * mm]});
            skFitSpline(sketch, "E241", {"points": [v(34.34, 18.75) * mm, v(34.06, 18.7) * mm, v(33.94, 18.75) * mm, v(33.58, 19.06) * mm]});
            skLineSegment(sketch, "E242", {"start": v(40.86, 28.72) * mm, "end": v(41.16, 28.31) * mm});
            skLineSegment(sketch, "E243", {"start": v(41.16, 28.31) * mm, "end": v(40.91, 28.12) * mm});
            skLineSegment(sketch, "E244", {"start": v(40.91, 28.12) * mm, "end": v(40.86, 28.72) * mm});
            skFitSpline(sketch, "E245", {"points": [v(-34.66, 19.28) * mm, v(-34.93, 19.33) * mm, v(-35.6, 19.9) * mm, v(-35.6, 20.08) * mm]});
            skFitSpline(sketch, "E246", {"points": [v(-35.6, 20.08) * mm, v(-35.6, 20.13) * mm, v(-35.76, 20.36) * mm, v(-35.95, 20.57) * mm]});
            skFitSpline(sketch, "E247", {"points": [v(-35.95, 20.57) * mm, v(-36.13, 20.8) * mm, v(-36.4, 21.12) * mm, v(-36.55, 21.3) * mm]});
            skFitSpline(sketch, "E248", {"points": [v(-36.55, 21.3) * mm, v(-36.7, 21.49) * mm, v(-36.96, 21.82) * mm, v(-37.15, 22.04) * mm]});
            skFitSpline(sketch, "E249", {"points": [v(-37.15, 22.04) * mm, v(-37.34, 22.25) * mm, v(-37.5, 22.47) * mm, v(-37.5, 22.51) * mm]});
            skFitSpline(sketch, "E250", {"points": [v(-37.5, 22.51) * mm, v(-37.5, 22.58) * mm, v(-37.8, 22.97) * mm, v(-38.4, 23.64) * mm]});
            skFitSpline(sketch, "E251", {"points": [v(-38.4, 23.64) * mm, v(-38.53, 23.8) * mm, v(-38.65, 23.97) * mm, v(-38.65, 24.01) * mm]});
            skFitSpline(sketch, "E252", {"points": [v(-38.65, 24.01) * mm, v(-38.65, 24.14) * mm, v(-39.43, 24.87) * mm, v(-39.57, 24.87) * mm]});
            skFitSpline(sketch, "E253", {"points": [v(-39.57, 24.87) * mm, v(-39.77, 24.87) * mm, v(-39.82, 25.07) * mm, v(-39.69, 25.32) * mm]});
            skFitSpline(sketch, "E254", {"points": [v(-39.69, 25.32) * mm, v(-39.47, 25.72) * mm, v(-39.02, 26.24) * mm, v(-38.89, 26.24) * mm]});
            skFitSpline(sketch, "E255", {"points": [v(-38.89, 26.24) * mm, v(-38.67, 26.24) * mm, v(-38.14, 25.77) * mm, v(-37.65, 25.14) * mm]});
            skFitSpline(sketch, "E256", {"points": [v(-37.65, 25.14) * mm, v(-37.48, 24.92) * mm, v(-37.2, 24.56) * mm, v(-37.02, 24.35) * mm]});
            skFitSpline(sketch, "E257", {"points": [v(-37.02, 24.35) * mm, v(-35.7, 22.7) * mm, v(-34.87, 21.62) * mm, v(-34.87, 21.54) * mm]});
            skFitSpline(sketch, "E258", {"points": [v(-34.87, 21.54) * mm, v(-34.87, 21.49) * mm, v(-34.75, 21.34) * mm, v(-34.6, 21.2) * mm]});
            skFitSpline(sketch, "E259", {"points": [v(-34.6, 21.2) * mm, v(-34.25, 20.87) * mm, v(-34.21, 21.01) * mm, v(-34.28, 22.47) * mm]});
            skFitSpline(sketch, "E260", {"points": [v(-34.28, 22.47) * mm, v(-34.34, 23.9) * mm, v(-34.43, 24.68) * mm, v(-34.56, 24.82) * mm]});
            skFitSpline(sketch, "E261", {"points": [v(-34.56, 24.82) * mm, v(-34.62, 24.87) * mm, v(-34.66, 25.07) * mm, v(-34.66, 25.26) * mm]});
            skFitSpline(sketch, "E262", {"points": [v(-34.66, 25.26) * mm, v(-34.66, 25.44) * mm, v(-34.7, 25.62) * mm, v(-34.75, 25.65) * mm]});
            skFitSpline(sketch, "E263", {"points": [v(-34.75, 25.65) * mm, v(-34.8, 25.69) * mm, v(-34.88, 25.92) * mm, v(-34.92, 26.18) * mm]});
            skFitSpline(sketch, "E264", {"points": [v(-34.92, 26.18) * mm, v(-34.95, 26.44) * mm, v(-35.03, 26.68) * mm, v(-35.09, 26.71) * mm]});
            skFitSpline(sketch, "E265", {"points": [v(-35.09, 26.71) * mm, v(-35.14, 26.75) * mm, v(-35.18, 26.9) * mm, v(-35.18, 27.03) * mm]});
            skFitSpline(sketch, "E266", {"points": [v(-35.18, 27.03) * mm, v(-35.18, 27.17) * mm, v(-35.23, 27.29) * mm, v(-35.29, 27.29) * mm]});
            skFitSpline(sketch, "E267", {"points": [v(-35.29, 27.29) * mm, v(-35.35, 27.29) * mm, v(-35.4, 27.38) * mm, v(-35.4, 27.5) * mm]});
            skFitSpline(sketch, "E268", {"points": [v(-35.4, 27.5) * mm, v(-35.4, 27.61) * mm, v(-35.44, 27.7) * mm, v(-35.5, 27.7) * mm]});
            skFitSpline(sketch, "E269", {"points": [v(-35.5, 27.7) * mm, v(-35.56, 27.7) * mm, v(-35.6, 27.78) * mm, v(-35.6, 27.87) * mm]});
            skFitSpline(sketch, "E270", {"points": [v(-35.6, 27.87) * mm, v(-35.6, 28.04) * mm, v(-36.1, 29.09) * mm, v(-36.23, 29.18) * mm]});
            skFitSpline(sketch, "E271", {"points": [v(-36.23, 29.18) * mm, v(-36.45, 29.34) * mm, v(-36.4, 29.72) * mm, v(-36.12, 30.08) * mm]});
            skFitSpline(sketch, "E272", {"points": [v(-36.12, 30.08) * mm, v(-35.95, 30.3) * mm, v(-35.81, 30.5) * mm, v(-35.81, 30.56) * mm]});
            skFitSpline(sketch, "E273", {"points": [v(-35.81, 30.56) * mm, v(-35.81, 30.72) * mm, v(-35.43, 30.65) * mm, v(-35.25, 30.46) * mm]});
            skFitSpline(sketch, "E274", {"points": [v(-35.25, 30.46) * mm, v(-35.16, 30.35) * mm, v(-35.08, 30.22) * mm, v(-35.08, 30.18) * mm]});
            skFitSpline(sketch, "E275", {"points": [v(-35.08, 30.18) * mm, v(-35.08, 30.13) * mm, v(-34.8, 29.8) * mm, v(-34.48, 29.44) * mm]});
            skFitSpline(sketch, "E276", {"points": [v(-34.48, 29.44) * mm, v(-34.14, 29.09) * mm, v(-33.59, 28.47) * mm, v(-33.24, 28.07) * mm]});
            skFitSpline(sketch, "E277", {"points": [v(-33.24, 28.07) * mm, v(-32.9, 27.67) * mm, v(-32.35, 27.05) * mm, v(-32.04, 26.69) * mm]});
            skFitSpline(sketch, "E278", {"points": [v(-32.04, 26.69) * mm, v(-31.72, 26.33) * mm, v(-31.3, 25.85) * mm, v(-31.13, 25.64) * mm]});
            skFitSpline(sketch, "E279", {"points": [v(-31.13, 25.64) * mm, v(-30.84, 25.3) * mm, v(-30.78, 25.27) * mm, v(-30.63, 25.39) * mm]});
            skFitSpline(sketch, "E280", {"points": [v(-30.63, 25.39) * mm, v(-30.54, 25.47) * mm, v(-30.46, 25.59) * mm, v(-30.46, 25.66) * mm]});
            skFitSpline(sketch, "E281", {"points": [v(-30.46, 25.66) * mm, v(-30.46, 25.73) * mm, v(-30.4, 25.85) * mm, v(-30.31, 25.91) * mm]});
            skFitSpline(sketch, "E282", {"points": [v(-30.31, 25.91) * mm, v(-30.2, 26.01) * mm, v(-30.1, 25.95) * mm, v(-29.84, 25.6) * mm]});
            skFitSpline(sketch, "E283", {"points": [v(-29.84, 25.6) * mm, v(-29.66, 25.35) * mm, v(-29.52, 25.1) * mm, v(-29.52, 25.03) * mm]});
            skFitSpline(sketch, "E284", {"points": [v(-29.52, 25.03) * mm, v(-29.52, 24.85) * mm, v(-29.77, 24.35) * mm, v(-29.86, 24.35) * mm]});
            skFitSpline(sketch, "E285", {"points": [v(-29.86, 24.35) * mm, v(-29.9, 24.35) * mm, v(-29.94, 24.28) * mm, v(-29.94, 24.2) * mm]});
            skFitSpline(sketch, "E286", {"points": [v(-29.94, 24.2) * mm, v(-29.94, 24.12) * mm, v(-30.09, 23.93) * mm, v(-30.27, 23.77) * mm]});
            skFitSpline(sketch, "E287", {"points": [v(-30.27, 23.77) * mm, v(-30.73, 23.39) * mm, v(-31.22, 23.47) * mm, v(-31.72, 24.03) * mm]});
            skFitSpline(sketch, "E288", {"points": [v(-31.72, 24.03) * mm, v(-32.17, 24.54) * mm, v(-33.2, 25.78) * mm, v(-33.31, 25.95) * mm]});
            skFitSpline(sketch, "E289", {"points": [v(-33.31, 25.95) * mm, v(-33.44, 26.17) * mm, v(-33.55, 25.94) * mm, v(-33.43, 25.69) * mm]});
            skFitSpline(sketch, "E290", {"points": [v(-33.43, 25.69) * mm, v(-33.1, 24.99) * mm, v(-32.94, 23.85) * mm, v(-32.95, 22.14) * mm]});
            skFitSpline(sketch, "E291", {"points": [v(-32.95, 22.14) * mm, v(-32.96, 20.32) * mm, v(-33.04, 19.88) * mm, v(-33.48, 19.49) * mm]});
            skFitSpline(sketch, "E292", {"points": [v(-33.48, 19.49) * mm, v(-33.7, 19.3) * mm, v(-34.21, 19.2) * mm, v(-34.66, 19.28) * mm]});
            skFitSpline(sketch, "E293", {"points": [v(28.8, 26.13) * mm, v(28.76, 26.2) * mm, v(28.67, 26.24) * mm, v(28.58, 26.24) * mm]});
            skFitSpline(sketch, "E294", {"points": [v(28.58, 26.24) * mm, v(28.34, 26.24) * mm, v(27.26, 26.79) * mm, v(26.92, 27.08) * mm]});
            skFitSpline(sketch, "E295", {"points": [v(26.92, 27.08) * mm, v(26.36, 27.56) * mm, v(25.5, 28.5) * mm, v(25.5, 28.61) * mm]});
            skFitSpline(sketch, "E296", {"points": [v(25.5, 28.61) * mm, v(25.5, 28.68) * mm, v(25.42, 28.8) * mm, v(25.33, 28.87) * mm]});
            skFitSpline(sketch, "E297", {"points": [v(25.33, 28.87) * mm, v(25.24, 28.94) * mm, v(25.03, 29.28) * mm, v(24.88, 29.62) * mm]});
            skFitSpline(sketch, "E298", {"points": [v(24.88, 29.62) * mm, v(24.6, 30.2) * mm, v(24.58, 30.22) * mm, v(24.38, 30.07) * mm]});
            skFitSpline(sketch, "E299", {"points": [v(24.38, 30.07) * mm, v(24.27, 29.99) * mm, v(24.08, 29.92) * mm, v(23.96, 29.92) * mm]});
            skFitSpline(sketch, "E300", {"points": [v(23.96, 29.92) * mm, v(23.71, 29.91) * mm, v(23.18, 30.14) * mm, v(23.18, 30.25) * mm]});
            skFitSpline(sketch, "E301", {"points": [v(23.18, 30.25) * mm, v(23.18, 30.3) * mm, v(23.12, 30.33) * mm, v(23.04, 30.33) * mm]});
            skFitSpline(sketch, "E302", {"points": [v(23.04, 30.33) * mm, v(22.78, 30.33) * mm, v(22.45, 30.8) * mm, v(22.45, 31.18) * mm]});
            skFitSpline(sketch, "E303", {"points": [v(22.45, 31.18) * mm, v(22.45, 31.5) * mm, v(22.55, 31.65) * mm, v(23.15, 32.24) * mm]});
            skFitSpline(sketch, "E304", {"points": [v(23.15, 32.24) * mm, v(23.54, 32.61) * mm, v(23.94, 32.97) * mm, v(24.04, 33.02) * mm]});
            skFitSpline(sketch, "E305", {"points": [v(24.04, 33.02) * mm, v(24.13, 33.07) * mm, v(24.42, 33.3) * mm, v(24.67, 33.53) * mm]});
            skFitSpline(sketch, "E306", {"points": [v(24.67, 33.53) * mm, v(24.92, 33.77) * mm, v(25.29, 34.08) * mm, v(25.5, 34.24) * mm]});
            skFitSpline(sketch, "E307", {"points": [v(25.5, 34.24) * mm, v(26.44, 34.96) * mm, v(28.1, 36.46) * mm, v(28.1, 36.6) * mm]});
            skFitSpline(sketch, "E308", {"points": [v(28.1, 36.6) * mm, v(28.13, 36.88) * mm, v(28.56, 36.84) * mm, v(28.85, 36.52) * mm]});
            skFitSpline(sketch, "E309", {"points": [v(28.85, 36.52) * mm, v(28.88, 36.49) * mm, v(29.05, 36.36) * mm, v(29.24, 36.23) * mm]});
            skFitSpline(sketch, "E310", {"points": [v(29.24, 36.23) * mm, v(29.58, 36) * mm, v(29.58, 35.99) * mm, v(29.4, 35.7) * mm]});
            skFitSpline(sketch, "E311", {"points": [v(29.4, 35.7) * mm, v(29.16, 35.34) * mm, v(28.57, 34.76) * mm, v(28.08, 34.43) * mm]});
            skFitSpline(sketch, "E312", {"points": [v(28.08, 34.43) * mm, v(27.87, 34.28) * mm, v(27.7, 34.13) * mm, v(27.7, 34.09) * mm]});
            skFitSpline(sketch, "E313", {"points": [v(27.7, 34.09) * mm, v(27.7, 34.04) * mm, v(27.5, 33.86) * mm, v(27.25, 33.69) * mm]});
            skFitSpline(sketch, "E314", {"points": [v(27.25, 33.69) * mm, v(27, 33.5) * mm, v(26.55, 33.13) * mm, v(26.25, 32.84) * mm]});
            skFitSpline(sketch, "E315", {"points": [v(26.25, 32.84) * mm, v(25.95, 32.56) * mm, v(25.67, 32.33) * mm, v(25.63, 32.33) * mm]});
            skFitSpline(sketch, "E316", {"points": [v(25.63, 32.33) * mm, v(25.6, 32.33) * mm, v(25.37, 32.15) * mm, v(25.13, 31.93) * mm]});
            skFitSpline(sketch, "E317", {"points": [v(25.13, 31.93) * mm, v(24.9, 31.72) * mm, v(24.57, 31.44) * mm, v(24.4, 31.32) * mm]});
            skFitSpline(sketch, "E318", {"points": [v(24.4, 31.32) * mm, v(24.08, 31.09) * mm, v(24.1, 30.86) * mm, v(24.44, 30.86) * mm]});
            skFitSpline(sketch, "E319", {"points": [v(24.44, 30.86) * mm, v(24.55, 30.86) * mm, v(24.67, 30.81) * mm, v(24.7, 30.75) * mm]});
            skFitSpline(sketch, "E320", {"points": [v(24.7, 30.75) * mm, v(24.8, 30.58) * mm, v(25.12, 30.63) * mm, v(25.36, 30.86) * mm]});
            skFitSpline(sketch, "E321", {"points": [v(25.36, 30.86) * mm, v(25.66, 31.14) * mm, v(25.73, 31.12) * mm, v(25.9, 30.73) * mm]});
            skFitSpline(sketch, "E322", {"points": [v(25.9, 30.73) * mm, v(26.04, 30.43) * mm, v(26.26, 30.06) * mm, v(26.93, 29.07) * mm]});
            skFitSpline(sketch, "E323", {"points": [v(26.93, 29.07) * mm, v(27.3, 28.5) * mm, v(28.3, 27.58) * mm, v(28.74, 27.38) * mm]});
            skFitSpline(sketch, "E324", {"points": [v(28.74, 27.38) * mm, v(29.08, 27.22) * mm, v(29.3, 27.18) * mm, v(29.63, 27.23) * mm]});
            skFitSpline(sketch, "E325", {"points": [v(29.63, 27.23) * mm, v(30.06, 27.3) * mm, v(30.53, 27.64) * mm, v(30.53, 27.88) * mm]});
            skFitSpline(sketch, "E326", {"points": [v(30.53, 27.88) * mm, v(30.53, 28.07) * mm, v(30.13, 28.82) * mm, v(29.94, 28.97) * mm]});
            skFitSpline(sketch, "E327", {"points": [v(29.94, 28.97) * mm, v(29.86, 29.04) * mm, v(29.8, 29.15) * mm, v(29.8, 29.2) * mm]});
            skFitSpline(sketch, "E328", {"points": [v(29.8, 29.2) * mm, v(29.8, 29.26) * mm, v(29.68, 29.45) * mm, v(29.53, 29.64) * mm]});
            skFitSpline(sketch, "E329", {"points": [v(29.53, 29.64) * mm, v(29.39, 29.82) * mm, v(29.23, 30.01) * mm, v(29.19, 30.07) * mm]});
            skFitSpline(sketch, "E330", {"points": [v(29.19, 30.07) * mm, v(29.02, 30.3) * mm, v(28.54, 31.35) * mm, v(28.42, 31.76) * mm]});
            skFitSpline(sketch, "E331", {"points": [v(28.42, 31.76) * mm, v(28.32, 32.13) * mm, v(28.33, 32.27) * mm, v(28.48, 32.69) * mm]});
            skFitSpline(sketch, "E332", {"points": [v(28.48, 32.69) * mm, v(28.69, 33.22) * mm, v(29.13, 33.66) * mm, v(29.57, 33.75) * mm]});
            skFitSpline(sketch, "E333", {"points": [v(29.57, 33.75) * mm, v(29.72, 33.78) * mm, v(29.94, 33.85) * mm, v(30.05, 33.89) * mm]});
            skFitSpline(sketch, "E334", {"points": [v(30.05, 33.89) * mm, v(30.31, 34) * mm, v(31.4, 33.84) * mm, v(32, 33.62) * mm]});
            skFitSpline(sketch, "E335", {"points": [v(32, 33.62) * mm, v(32.85, 33.31) * mm, v(33.84, 32.5) * mm, v(34.56, 31.55) * mm]});
            skFitSpline(sketch, "E336", {"points": [v(34.56, 31.55) * mm, v(34.9, 31.1) * mm, v(35.46, 30.08) * mm, v(35.46, 29.92) * mm]});
            skFitSpline(sketch, "E337", {"points": [v(35.46, 29.92) * mm, v(35.46, 29.87) * mm, v(35.19, 29.68) * mm, v(34.85, 29.51) * mm]});
            skFitSpline(sketch, "E338", {"points": [v(34, 29.77) * mm, v(33.86, 30.08) * mm, v(33.71, 30.33) * mm, v(33.66, 30.33) * mm]});
            skFitSpline(sketch, "E339", {"points": [v(33.66, 30.33) * mm, v(33.61, 30.33) * mm, v(33.57, 30.4) * mm, v(33.57, 30.46) * mm]});
            skFitSpline(sketch, "E340", {"points": [v(33.57, 30.46) * mm, v(33.57, 30.54) * mm, v(33.41, 30.77) * mm, v(33.22, 30.98) * mm]});
            skFitSpline(sketch, "E341", {"points": [v(33.22, 30.98) * mm, v(33.03, 31.19) * mm, v(32.84, 31.44) * mm, v(32.8, 31.53) * mm]});
            skFitSpline(sketch, "E342", {"points": [v(32.8, 31.53) * mm, v(32.77, 31.63) * mm, v(32.65, 31.73) * mm, v(32.55, 31.77) * mm]});
            skFitSpline(sketch, "E343", {"points": [v(32.55, 31.77) * mm, v(32.45, 31.8) * mm, v(32.14, 32.04) * mm, v(31.86, 32.3) * mm]});
            skFitSpline(sketch, "E344", {"points": [v(31.86, 32.3) * mm, v(31.44, 32.66) * mm, v(31.27, 32.75) * mm, v(30.93, 32.75) * mm]});
            skFitSpline(sketch, "E345", {"points": [v(30.93, 32.75) * mm, v(30.36, 32.75) * mm, v(30, 32.5) * mm, v(30, 32.09) * mm]});
            skFitSpline(sketch, "E346", {"points": [v(30, 32.09) * mm, v(30, 31.73) * mm, v(30.35, 30.95) * mm, v(30.59, 30.75) * mm]});
            skFitSpline(sketch, "E347", {"points": [v(30.59, 30.75) * mm, v(30.67, 30.68) * mm, v(30.74, 30.58) * mm, v(30.74, 30.52) * mm]});
            skFitSpline(sketch, "E348", {"points": [v(30.74, 30.52) * mm, v(30.74, 30.46) * mm, v(30.86, 30.27) * mm, v(31, 30.09) * mm]});
            skFitSpline(sketch, "E349", {"points": [v(31, 30.09) * mm, v(31.38, 29.62) * mm, v(31.4, 29.58) * mm, v(31.57, 29.26) * mm]});
            skFitSpline(sketch, "E350", {"points": [v(31.57, 29.26) * mm, v(31.65, 29.1) * mm, v(31.76, 28.97) * mm, v(31.8, 28.97) * mm]});
            skFitSpline(sketch, "E351", {"points": [v(31.8, 28.97) * mm, v(31.85, 28.97) * mm, v(31.9, 28.85) * mm, v(31.9, 28.71) * mm]});
            skFitSpline(sketch, "E352", {"points": [v(31.9, 28.71) * mm, v(31.9, 28.57) * mm, v(31.94, 28.43) * mm, v(32, 28.4) * mm]});
            skFitSpline(sketch, "E353", {"points": [v(32, 28.4) * mm, v(32.15, 28.3) * mm, v(32.13, 27.54) * mm, v(31.97, 27.26) * mm]});
            skFitSpline(sketch, "E354", {"points": [v(31.97, 27.26) * mm, v(31.8, 26.94) * mm, v(31.17, 26.36) * mm, v(30.8, 26.18) * mm]});
            skFitSpline(sketch, "E355", {"points": [v(30.8, 26.18) * mm, v(30.45, 26) * mm, v(28.9, 25.97) * mm, v(28.8, 26.13) * mm]});
            skLineSegment(sketch, "E356", {"start": v(34.85, 29.51) * mm, "end": v(34.24, 29.2) * mm});
            skLineSegment(sketch, "E357", {"start": v(34.24, 29.2) * mm, "end": v(34, 29.77) * mm});
            skLineSegment(sketch, "E358", {"start": v(34, 29.77) * mm, "end": v(34.85, 29.51) * mm});
            skFitSpline(sketch, "E359", {"points": [v(-29.3, 26.82) * mm, v(-29.73, 27.05) * mm, v(-30.21, 27.57) * mm, v(-30.43, 28.02) * mm]});
            skFitSpline(sketch, "E360", {"points": [v(-30.43, 28.02) * mm, v(-30.47, 28.1) * mm, v(-30.75, 28.57) * mm, v(-31.06, 29.04) * mm]});
            skFitSpline(sketch, "E361", {"points": [v(-31.06, 29.04) * mm, v(-31.36, 29.5) * mm, v(-31.62, 29.94) * mm, v(-31.62, 30) * mm]});
            skFitSpline(sketch, "E362", {"points": [v(-31.62, 30) * mm, v(-31.62, 30.07) * mm, v(-31.65, 30.12) * mm, v(-31.7, 30.12) * mm]});
            skFitSpline(sketch, "E363", {"points": [v(-31.7, 30.12) * mm, v(-31.78, 30.12) * mm, v(-31.83, 30.2) * mm, v(-32.22, 31) * mm]});
            skFitSpline(sketch, "E364", {"points": [v(-32.22, 31) * mm, v(-32.35, 31.26) * mm, v(-32.5, 31.5) * mm, v(-32.57, 31.55) * mm]});
            skFitSpline(sketch, "E365", {"points": [v(-32.57, 31.55) * mm, v(-32.63, 31.58) * mm, v(-32.89, 31.42) * mm, v(-33.14, 31.17) * mm]});
            skFitSpline(sketch, "E366", {"points": [v(-33.14, 31.17) * mm, v(-33.39, 30.93) * mm, v(-33.64, 30.76) * mm, v(-33.7, 30.8) * mm]});
            skFitSpline(sketch, "E367", {"points": [v(-33.7, 30.8) * mm, v(-33.75, 30.83) * mm, v(-33.92, 31.09) * mm, v(-34.07, 31.37) * mm]});
            skFitSpline(sketch, "E368", {"points": [v(-33.54, 33.11) * mm, v(-33.66, 33.29) * mm, v(-33.78, 33.45) * mm, v(-33.82, 33.48) * mm]});
            skFitSpline(sketch, "E369", {"points": [v(-33.82, 33.48) * mm, v(-33.85, 33.51) * mm, v(-33.93, 33.67) * mm, v(-34, 33.83) * mm]});
            skFitSpline(sketch, "E370", {"points": [v(-34, 33.83) * mm, v(-34.12, 34.1) * mm, v(-34.11, 34.13) * mm, v(-33.86, 34.22) * mm]});
            skFitSpline(sketch, "E371", {"points": [v(-33.86, 34.22) * mm, v(-33.71, 34.28) * mm, v(-33.57, 34.4) * mm, v(-33.54, 34.5) * mm]});
            skFitSpline(sketch, "E372", {"points": [v(-33.54, 34.5) * mm, v(-33.5, 34.67) * mm, v(-32.9, 35.03) * mm, v(-32.83, 34.94) * mm]});
            skFitSpline(sketch, "E373", {"points": [v(-32.83, 34.94) * mm, v(-32.82, 34.92) * mm, v(-32.72, 34.72) * mm, v(-32.62, 34.5) * mm]});
            skFitSpline(sketch, "E374", {"points": [v(-32.62, 34.5) * mm, v(-32.52, 34.28) * mm, v(-32.37, 34.07) * mm, v(-32.28, 34.04) * mm]});
            skFitSpline(sketch, "E375", {"points": [v(-32.28, 34.04) * mm, v(-32.17, 34) * mm, v(-31.8, 34.3) * mm, v(-31.16, 34.94) * mm]});
            skFitSpline(sketch, "E376", {"points": [v(-31.16, 34.94) * mm, v(-30.63, 35.46) * mm, v(-30.16, 35.9) * mm, v(-30.1, 35.9) * mm]});
            skFitSpline(sketch, "E377", {"points": [v(-30.1, 35.9) * mm, v(-29.92, 35.9) * mm, v(-29.41, 35.1) * mm, v(-29.41, 34.82) * mm]});
            skFitSpline(sketch, "E378", {"points": [v(-29.41, 34.82) * mm, v(-29.41, 34.74) * mm, v(-29.86, 34.23) * mm, v(-30.4, 33.69) * mm]});
            skFitSpline(sketch, "E379", {"points": [v(-30.4, 33.69) * mm, v(-31.4, 32.7) * mm, v(-31.54, 32.47) * mm, v(-31.25, 32.22) * mm]});
            skFitSpline(sketch, "E380", {"points": [v(-31.25, 32.22) * mm, v(-31.16, 32.15) * mm, v(-31.1, 32.03) * mm, v(-31.1, 31.96) * mm]});
            skFitSpline(sketch, "E381", {"points": [v(-31.1, 31.96) * mm, v(-31.1, 31.88) * mm, v(-31.05, 31.8) * mm, v(-31.01, 31.78) * mm]});
            skFitSpline(sketch, "E382", {"points": [v(-31.01, 31.78) * mm, v(-30.92, 31.74) * mm, v(-30.46, 31.1) * mm, v(-30.46, 31.01) * mm]});
            skFitSpline(sketch, "E383", {"points": [v(-30.46, 31.01) * mm, v(-30.46, 30.98) * mm, v(-30.13, 30.43) * mm, v(-29.73, 29.8) * mm]});
            skFitSpline(sketch, "E384", {"points": [v(-29.73, 29.8) * mm, v(-29.32, 29.16) * mm, v(-29, 28.6) * mm, v(-29, 28.54) * mm]});
            skFitSpline(sketch, "E385", {"points": [v(-29, 28.54) * mm, v(-29, 28.49) * mm, v(-28.95, 28.44) * mm, v(-28.9, 28.44) * mm]});
            skFitSpline(sketch, "E386", {"points": [v(-28.9, 28.44) * mm, v(-28.85, 28.44) * mm, v(-28.76, 28.32) * mm, v(-28.7, 28.18) * mm]});
            skFitSpline(sketch, "E387", {"points": [v(-28.7, 28.18) * mm, v(-28.5, 27.75) * mm, v(-28.15, 27.84) * mm, v(-27.56, 28.48) * mm]});
            skFitSpline(sketch, "E388", {"points": [v(-27.56, 28.48) * mm, v(-26.33, 29.81) * mm, v(-26.18, 30.23) * mm, v(-26.62, 31.14) * mm]});
            skFitSpline(sketch, "E389", {"points": [v(-26.62, 31.14) * mm, v(-26.93, 31.77) * mm, v(-27.2, 32.43) * mm, v(-27.42, 33.02) * mm]});
            skFitSpline(sketch, "E390", {"points": [v(-27.42, 33.02) * mm, v(-27.65, 33.65) * mm, v(-27.85, 34.14) * mm, v(-28.1, 34.68) * mm]});
            skFitSpline(sketch, "E391", {"points": [v(-28.1, 34.68) * mm, v(-28.2, 34.85) * mm, v(-28.26, 35.03) * mm, v(-28.26, 35.08) * mm]});
            skFitSpline(sketch, "E392", {"points": [v(-28.26, 35.08) * mm, v(-28.26, 35.18) * mm, v(-28.5, 35.79) * mm, v(-28.68, 36.13) * mm]});
            skFitSpline(sketch, "E393", {"points": [v(-28.68, 36.13) * mm, v(-28.74, 36.23) * mm, v(-28.78, 36.38) * mm, v(-28.78, 36.47) * mm]});
            skFitSpline(sketch, "E394", {"points": [v(-28.78, 36.47) * mm, v(-28.78, 36.56) * mm, v(-28.82, 36.63) * mm, v(-28.86, 36.63) * mm]});
            skFitSpline(sketch, "E395", {"points": [v(-28.86, 36.63) * mm, v(-28.9, 36.63) * mm, v(-29.03, 36.92) * mm, v(-29.14, 37.27) * mm]});
            skFitSpline(sketch, "E396", {"points": [v(-29.14, 37.27) * mm, v(-29.25, 37.62) * mm, v(-29.38, 37.93) * mm, v(-29.43, 37.96) * mm]});
            skFitSpline(sketch, "E397", {"points": [v(-29.43, 37.96) * mm, v(-29.48, 37.98) * mm, v(-29.52, 38.08) * mm, v(-29.52, 38.17) * mm]});
            skFitSpline(sketch, "E398", {"points": [v(-29.52, 38.17) * mm, v(-29.52, 38.26) * mm, v(-29.68, 38.57) * mm, v(-29.9, 38.86) * mm]});
            skLineSegment(sketch, "E399", {"start": v(-34.07, 31.37) * mm, "end": v(-34.33, 31.88) * mm});
            skLineSegment(sketch, "E400", {"start": v(-34.33, 31.88) * mm, "end": v(-33.83, 32.34) * mm});
            skLineSegment(sketch, "E401", {"start": v(-33.83, 32.34) * mm, "end": v(-33.32, 32.8) * mm});
            skLineSegment(sketch, "E402", {"start": v(-33.32, 32.8) * mm, "end": v(-33.54, 33.11) * mm});
            skFitSpline(sketch, "E403", {"points": [v(-30.05, 39.58) * mm, v(-29.94, 39.7) * mm, v(-29.8, 39.78) * mm, v(-29.75, 39.78) * mm]});
            skFitSpline(sketch, "E404", {"points": [v(-29.75, 39.78) * mm, v(-29.7, 39.78) * mm, v(-29.57, 39.87) * mm, v(-29.46, 40) * mm]});
            skFitSpline(sketch, "E405", {"points": [v(-29.46, 40) * mm, v(-29.21, 40.27) * mm, v(-28.9, 40.26) * mm, v(-28.78, 39.96) * mm]});
            skFitSpline(sketch, "E406", {"points": [v(-28.78, 39.96) * mm, v(-28.67, 39.72) * mm, v(-28.45, 39.35) * mm, v(-28.36, 39.26) * mm]});
            skFitSpline(sketch, "E407", {"points": [v(-28.36, 39.26) * mm, v(-28.33, 39.23) * mm, v(-28.26, 39.08) * mm, v(-28.2, 38.94) * mm]});
            skFitSpline(sketch, "E408", {"points": [v(-28.2, 38.94) * mm, v(-28.13, 38.8) * mm, v(-27.98, 38.47) * mm, v(-27.86, 38.2) * mm]});
            skFitSpline(sketch, "E409", {"points": [v(-27.86, 38.2) * mm, v(-27.74, 37.95) * mm, v(-27.6, 37.62) * mm, v(-27.57, 37.47) * mm]});
            skFitSpline(sketch, "E410", {"points": [v(-27.57, 37.47) * mm, v(-27.53, 37.33) * mm, v(-27.44, 37.05) * mm, v(-27.36, 36.87) * mm]});
            skFitSpline(sketch, "E411", {"points": [v(-27.36, 36.87) * mm, v(-27.27, 36.68) * mm, v(-27.13, 36.35) * mm, v(-27.04, 36.13) * mm]});
            skFitSpline(sketch, "E412", {"points": [v(-27.04, 36.13) * mm, v(-26.95, 35.92) * mm, v(-26.84, 35.67) * mm, v(-26.8, 35.58) * mm]});
            skFitSpline(sketch, "E413", {"points": [v(-26.8, 35.58) * mm, v(-26.75, 35.49) * mm, v(-26.67, 35.25) * mm, v(-26.63, 35.06) * mm]});
            skFitSpline(sketch, "E414", {"points": [v(-26.63, 35.06) * mm, v(-26.59, 34.86) * mm, v(-26.51, 34.62) * mm, v(-26.47, 34.53) * mm]});
            skFitSpline(sketch, "E415", {"points": [v(-26.47, 34.53) * mm, v(-26.42, 34.45) * mm, v(-26.35, 34.28) * mm, v(-26.32, 34.17) * mm]});
            skFitSpline(sketch, "E416", {"points": [v(-26.32, 34.17) * mm, v(-26.2, 33.8) * mm, v(-26.05, 34.16) * mm, v(-25.95, 35.06) * mm]});
            skFitSpline(sketch, "E417", {"points": [v(-25.95, 35.06) * mm, v(-25.86, 35.92) * mm, v(-25.78, 36.36) * mm, v(-25.53, 37.37) * mm]});
            skFitSpline(sketch, "E418", {"points": [v(-25.53, 37.37) * mm, v(-25.41, 37.87) * mm, v(-25.39, 37.93) * mm, v(-24.96, 38.86) * mm]});
            skFitSpline(sketch, "E419", {"points": [v(-24.96, 38.86) * mm, v(-24.6, 39.63) * mm, v(-24.03, 40.2) * mm, v(-23.63, 40.2) * mm]});
            skFitSpline(sketch, "E420", {"points": [v(-23.63, 40.2) * mm, v(-23.09, 40.2) * mm, v(-22.38, 39.68) * mm, v(-22.38, 39.29) * mm]});
            skFitSpline(sketch, "E421", {"points": [v(-22.38, 39.29) * mm, v(-22.38, 39.16) * mm, v(-22.33, 39.05) * mm, v(-22.27, 39.05) * mm]});
            skFitSpline(sketch, "E422", {"points": [v(-22.27, 39.05) * mm, v(-22.21, 39.05) * mm, v(-22.17, 38.93) * mm, v(-22.17, 38.79) * mm]});
            skFitSpline(sketch, "E423", {"points": [v(-22.17, 38.79) * mm, v(-22.17, 38.65) * mm, v(-22.13, 38.5) * mm, v(-22.08, 38.48) * mm]});
            skFitSpline(sketch, "E424", {"points": [v(-22.08, 38.48) * mm, v(-22.03, 38.45) * mm, v(-21.95, 38.23) * mm, v(-21.92, 38) * mm]});
            skFitSpline(sketch, "E425", {"points": [v(-21.92, 38) * mm, v(-21.88, 37.76) * mm, v(-21.8, 37.49) * mm, v(-21.76, 37.39) * mm]});
            skFitSpline(sketch, "E426", {"points": [v(-21.76, 37.39) * mm, v(-21.6, 37.07) * mm, v(-21.45, 36.7) * mm, v(-21.32, 36.26) * mm]});
            skFitSpline(sketch, "E427", {"points": [v(-21.32, 36.26) * mm, v(-21.25, 36.03) * mm, v(-21.16, 35.75) * mm, v(-21.11, 35.63) * mm]});
            skFitSpline(sketch, "E428", {"points": [v(-21.11, 35.63) * mm, v(-21.07, 35.52) * mm, v(-20.95, 35.16) * mm, v(-20.84, 34.85) * mm]});
            skFitSpline(sketch, "E429", {"points": [v(-20.84, 34.85) * mm, v(-20.74, 34.53) * mm, v(-20.62, 34.22) * mm, v(-20.57, 34.17) * mm]});
            skFitSpline(sketch, "E430", {"points": [v(-20.57, 34.17) * mm, v(-20.53, 34.11) * mm, v(-20.49, 33.98) * mm, v(-20.49, 33.88) * mm]});
            skFitSpline(sketch, "E431", {"points": [v(-20.49, 33.88) * mm, v(-20.49, 33.62) * mm, v(-20.36, 33.64) * mm, v(-20.07, 33.95) * mm]});
            skFitSpline(sketch, "E432", {"points": [v(-20.07, 33.95) * mm, v(-19.75, 34.29) * mm, v(-19.54, 34.3) * mm, v(-19.54, 33.96) * mm]});
            skFitSpline(sketch, "E433", {"points": [v(-19.54, 33.96) * mm, v(-19.54, 33.82) * mm, v(-19.5, 33.67) * mm, v(-19.44, 33.64) * mm]});
            skFitSpline(sketch, "E434", {"points": [v(-19.44, 33.64) * mm, v(-19.25, 33.52) * mm, v(-19.33, 33) * mm, v(-19.57, 32.77) * mm]});
            skFitSpline(sketch, "E435", {"points": [v(-19.57, 32.77) * mm, v(-19.7, 32.65) * mm, v(-20.04, 32.42) * mm, v(-20.32, 32.28) * mm]});
            skFitSpline(sketch, "E436", {"points": [v(-20.32, 32.28) * mm, v(-20.77, 32.04) * mm, v(-20.86, 32.02) * mm, v(-21.13, 32.14) * mm]});
            skFitSpline(sketch, "E437", {"points": [v(-21.13, 32.14) * mm, v(-21.3, 32.21) * mm, v(-21.5, 32.44) * mm, v(-21.6, 32.64) * mm]});
            skFitSpline(sketch, "E438", {"points": [v(-21.6, 32.64) * mm, v(-21.7, 32.84) * mm, v(-21.82, 33.1) * mm, v(-21.87, 33.2) * mm]});
            skFitSpline(sketch, "E439", {"points": [v(-21.87, 33.2) * mm, v(-21.92, 33.3) * mm, v(-21.96, 33.45) * mm, v(-21.96, 33.53) * mm]});
            skFitSpline(sketch, "E440", {"points": [v(-21.96, 33.53) * mm, v(-21.96, 33.62) * mm, v(-22, 33.79) * mm, v(-22.06, 33.9) * mm]});
            skFitSpline(sketch, "E441", {"points": [v(-22.06, 33.9) * mm, v(-22.12, 34.02) * mm, v(-22.21, 34.2) * mm, v(-22.27, 34.32) * mm]});
            skFitSpline(sketch, "E442", {"points": [v(-22.27, 34.32) * mm, v(-22.33, 34.43) * mm, v(-22.38, 34.61) * mm, v(-22.38, 34.72) * mm]});
            skFitSpline(sketch, "E443", {"points": [v(-22.38, 34.72) * mm, v(-22.38, 34.82) * mm, v(-22.41, 34.95) * mm, v(-22.46, 35) * mm]});
            skFitSpline(sketch, "E444", {"points": [v(-22.46, 35) * mm, v(-22.5, 35.06) * mm, v(-22.63, 35.4) * mm, v(-22.73, 35.74) * mm]});
            skFitSpline(sketch, "E445", {"points": [v(-22.73, 35.74) * mm, v(-22.84, 36.09) * mm, v(-22.97, 36.45) * mm, v(-23.02, 36.55) * mm]});
            skFitSpline(sketch, "E446", {"points": [v(-23.02, 36.55) * mm, v(-23.07, 36.65) * mm, v(-23.11, 36.8) * mm, v(-23.11, 36.9) * mm]});
            skFitSpline(sketch, "E447", {"points": [v(-23.11, 36.9) * mm, v(-23.11, 36.98) * mm, v(-23.16, 37.15) * mm, v(-23.22, 37.26) * mm]});
            skFitSpline(sketch, "E448", {"points": [v(-23.22, 37.26) * mm, v(-23.27, 37.38) * mm, v(-23.37, 37.56) * mm, v(-23.43, 37.68) * mm]});
            skFitSpline(sketch, "E449", {"points": [v(-23.43, 37.68) * mm, v(-23.48, 37.8) * mm, v(-23.53, 37.98) * mm, v(-23.53, 38.1) * mm]});
            skFitSpline(sketch, "E450", {"points": [v(-23.53, 38.1) * mm, v(-23.53, 38.22) * mm, v(-23.57, 38.31) * mm, v(-23.62, 38.31) * mm]});
            skFitSpline(sketch, "E451", {"points": [v(-23.62, 38.31) * mm, v(-23.73, 38.31) * mm, v(-24.06, 37.5) * mm, v(-24.06, 37.24) * mm]});
            skFitSpline(sketch, "E452", {"points": [v(-24.06, 37.24) * mm, v(-24.06, 37.14) * mm, v(-24.1, 37.04) * mm, v(-24.15, 37) * mm]});
            skFitSpline(sketch, "E453", {"points": [v(-24.15, 37) * mm, v(-24.24, 36.95) * mm, v(-24.3, 36.68) * mm, v(-24.5, 35.58) * mm]});
            skFitSpline(sketch, "E454", {"points": [v(-24.5, 35.58) * mm, v(-24.7, 34.34) * mm, v(-24.76, 33.35) * mm, v(-24.72, 31.4) * mm]});
            skFitSpline(sketch, "E455", {"points": [v(-24.72, 31.4) * mm, v(-24.7, 29.77) * mm, v(-24.71, 29.39) * mm, v(-24.83, 29.39) * mm]});
            skFitSpline(sketch, "E456", {"points": [v(-24.83, 29.39) * mm, v(-24.99, 29.39) * mm, v(-25.95, 28.47) * mm, v(-25.95, 28.32) * mm]});
            skFitSpline(sketch, "E457", {"points": [v(-25.95, 28.32) * mm, v(-25.95, 28.1) * mm, v(-27.08, 27.04) * mm, v(-27.57, 26.8) * mm]});
            skFitSpline(sketch, "E458", {"points": [v(-27.57, 26.8) * mm, v(-28.22, 26.49) * mm, v(-28.7, 26.5) * mm, v(-29.3, 26.82) * mm]});
            skLineSegment(sketch, "E459", {"start": v(-29.9, 38.86) * mm, "end": v(-30.27, 39.38) * mm});
            skLineSegment(sketch, "E460", {"start": v(-30.27, 39.38) * mm, "end": v(-30.05, 39.58) * mm});
            skFitSpline(sketch, "E461", {"points": [v(20.87, 31.9) * mm, v(20.78, 31.94) * mm, v(20.53, 32.07) * mm, v(20.31, 32.18) * mm]});
            skFitSpline(sketch, "E462", {"points": [v(20.31, 32.18) * mm, v(20.06, 32.3) * mm, v(19.86, 32.49) * mm, v(19.78, 32.69) * mm]});
            skFitSpline(sketch, "E463", {"points": [v(19.78, 32.69) * mm, v(19.66, 32.97) * mm, v(19.67, 33.06) * mm, v(19.87, 33.4) * mm]});
            skFitSpline(sketch, "E464", {"points": [v(19.87, 33.4) * mm, v(19.99, 33.61) * mm, v(21, 34.71) * mm, v(22.12, 35.84) * mm]});
            skFitSpline(sketch, "E465", {"points": [v(22.12, 35.84) * mm, v(23.24, 36.97) * mm, v(24.13, 37.92) * mm, v(24.1, 37.95) * mm]});
            skFitSpline(sketch, "E466", {"points": [v(24.1, 37.95) * mm, v(24.03, 38.02) * mm, v(22.42, 37.79) * mm, v(22.21, 37.67) * mm]});
            skFitSpline(sketch, "E467", {"points": [v(22.21, 37.67) * mm, v(22.11, 37.62) * mm, v(21.95, 37.58) * mm, v(21.84, 37.58) * mm]});
            skFitSpline(sketch, "E468", {"points": [v(21.84, 37.58) * mm, v(21.74, 37.58) * mm, v(21.33, 37.46) * mm, v(20.93, 37.31) * mm]});
            skFitSpline(sketch, "E469", {"points": [v(20.93, 37.31) * mm, v(20.54, 37.17) * mm, v(20.12, 37.05) * mm, v(20.02, 37.05) * mm]});
            skFitSpline(sketch, "E470", {"points": [v(20.02, 37.05) * mm, v(19.9, 37.05) * mm, v(19.82, 37) * mm, v(19.82, 36.95) * mm]});
            skFitSpline(sketch, "E471", {"points": [v(19.82, 36.95) * mm, v(19.82, 36.89) * mm, v(19.75, 36.84) * mm, v(19.67, 36.84) * mm]});
            skFitSpline(sketch, "E472", {"points": [v(19.67, 36.84) * mm, v(19.48, 36.84) * mm, v(17.58, 35.9) * mm, v(17.53, 35.77) * mm]});
            skFitSpline(sketch, "E473", {"points": [v(17.53, 35.77) * mm, v(17.51, 35.73) * mm, v(17.45, 35.69) * mm, v(17.4, 35.69) * mm]});
            skFitSpline(sketch, "E474", {"points": [v(17.4, 35.69) * mm, v(17.33, 35.69) * mm, v(16.96, 35.47) * mm, v(16.56, 35.21) * mm]});
            skFitSpline(sketch, "E475", {"points": [v(16.56, 35.21) * mm, v(16.15, 34.95) * mm, v(15.79, 34.74) * mm, v(15.75, 34.74) * mm]});
            skFitSpline(sketch, "E476", {"points": [v(15.75, 34.74) * mm, v(15.6, 34.74) * mm, v(14.68, 35.36) * mm, v(14.68, 35.46) * mm]});
            skFitSpline(sketch, "E477", {"points": [v(14.68, 35.46) * mm, v(14.68, 35.52) * mm, v(14.94, 35.82) * mm, v(15.26, 36.14) * mm]});
            skFitSpline(sketch, "E478", {"points": [v(15.26, 36.14) * mm, v(15.57, 36.47) * mm, v(15.83, 36.76) * mm, v(15.83, 36.8) * mm]});
            skFitSpline(sketch, "E479", {"points": [v(15.83, 36.8) * mm, v(15.83, 36.84) * mm, v(16.12, 37.19) * mm, v(16.46, 37.57) * mm]});
            skFitSpline(sketch, "E480", {"points": [v(16.46, 37.57) * mm, v(16.81, 37.95) * mm, v(17.35, 38.54) * mm, v(17.66, 38.89) * mm]});
            skFitSpline(sketch, "E481", {"points": [v(17.66, 38.89) * mm, v(17.97, 39.23) * mm, v(18.48, 39.8) * mm, v(18.8, 40.15) * mm]});
            skFitSpline(sketch, "E482", {"points": [v(18.8, 40.15) * mm, v(19.48, 40.9) * mm, v(19.82, 41.38) * mm, v(19.82, 41.6) * mm]});
            skFitSpline(sketch, "E483", {"points": [v(19.82, 41.6) * mm, v(19.82, 41.85) * mm, v(20.13, 41.9) * mm, v(20.43, 41.7) * mm]});
            skFitSpline(sketch, "E484", {"points": [v(20.43, 41.7) * mm, v(20.59, 41.59) * mm, v(20.84, 41.44) * mm, v(21, 41.36) * mm]});
            skFitSpline(sketch, "E485", {"points": [v(21, 41.36) * mm, v(21.16, 41.28) * mm, v(21.3, 41.15) * mm, v(21.3, 41.08) * mm]});
            skFitSpline(sketch, "E486", {"points": [v(21.3, 41.08) * mm, v(21.3, 40.88) * mm, v(20.96, 40.36) * mm, v(20.52, 39.89) * mm]});
            skFitSpline(sketch, "E487", {"points": [v(20.52, 39.89) * mm, v(20.3, 39.66) * mm, v(20.13, 39.44) * mm, v(20.13, 39.4) * mm]});
            skFitSpline(sketch, "E488", {"points": [v(20.13, 39.4) * mm, v(20.13, 39.35) * mm, v(19.9, 39.07) * mm, v(19.6, 38.78) * mm]});
            skFitSpline(sketch, "E489", {"points": [v(19.6, 38.78) * mm, v(18.91, 38.08) * mm, v(18.92, 37.9) * mm, v(19.63, 38.3) * mm]});
            skFitSpline(sketch, "E490", {"points": [v(19.63, 38.3) * mm, v(20.06, 38.53) * mm, v(21, 38.84) * mm, v(21.28, 38.84) * mm]});
            skFitSpline(sketch, "E491", {"points": [v(21.28, 38.84) * mm, v(21.4, 38.84) * mm, v(21.5, 38.88) * mm, v(21.5, 38.94) * mm]});
            skFitSpline(sketch, "E492", {"points": [v(21.5, 38.94) * mm, v(21.5, 39) * mm, v(21.68, 39.05) * mm, v(21.9, 39.05) * mm]});
            skFitSpline(sketch, "E493", {"points": [v(21.9, 39.05) * mm, v(22.12, 39.05) * mm, v(22.35, 39.1) * mm, v(22.4, 39.15) * mm]});
            skFitSpline(sketch, "E494", {"points": [v(22.4, 39.15) * mm, v(22.47, 39.22) * mm, v(23.11, 39.27) * mm, v(23.9, 39.29) * mm]});
            skFitSpline(sketch, "E495", {"points": [v(23.9, 39.29) * mm, v(25.2, 39.3) * mm, v(25.29, 39.3) * mm, v(25.51, 39.07) * mm]});
            skFitSpline(sketch, "E496", {"points": [v(25.51, 39.07) * mm, v(25.83, 38.76) * mm, v(26.02, 37.93) * mm, v(25.85, 37.6) * mm]});
            skFitSpline(sketch, "E497", {"points": [v(25.85, 37.6) * mm, v(25.78, 37.46) * mm, v(25.03, 36.66) * mm, v(24.18, 35.81) * mm]});
            skFitSpline(sketch, "E498", {"points": [v(24.18, 35.81) * mm, v(21.62, 33.25) * mm, v(21.47, 33.09) * mm, v(21.54, 32.98) * mm]});
            skFitSpline(sketch, "E499", {"points": [v(21.54, 32.98) * mm, v(21.57, 32.93) * mm, v(21.74, 32.85) * mm, v(21.92, 32.82) * mm]});
            skFitSpline(sketch, "E500", {"points": [v(21.92, 32.82) * mm, v(22.32, 32.74) * mm, v(22.32, 32.64) * mm, v(21.91, 32.17) * mm]});
            skFitSpline(sketch, "E501", {"points": [v(21.91, 32.17) * mm, v(21.58, 31.8) * mm, v(21.23, 31.7) * mm, v(20.87, 31.9) * mm]});
            skFitSpline(sketch, "E502", {"points": [v(-17.81, 34.32) * mm, v(-17.85, 34.38) * mm, v(-17.96, 34.43) * mm, v(-18.06, 34.43) * mm]});
            skFitSpline(sketch, "E503", {"points": [v(-18.06, 34.43) * mm, v(-18.38, 34.43) * mm, v(-18.88, 34.73) * mm, v(-19.27, 35.16) * mm]});
            skFitSpline(sketch, "E504", {"points": [v(-19.27, 35.16) * mm, v(-19.67, 35.6) * mm, v(-20.07, 36.35) * mm, v(-20.07, 36.64) * mm]});
            skFitSpline(sketch, "E505", {"points": [v(-20.07, 36.64) * mm, v(-20.07, 36.75) * mm, v(-20.12, 36.86) * mm, v(-20.17, 36.9) * mm]});
            skFitSpline(sketch, "E506", {"points": [v(-20.17, 36.9) * mm, v(-20.23, 36.93) * mm, v(-20.28, 37.42) * mm, v(-20.28, 38) * mm]});
            skFitSpline(sketch, "E507", {"points": [v(-20.28, 38) * mm, v(-20.28, 38.57) * mm, v(-20.23, 39.06) * mm, v(-20.17, 39.1) * mm]});
            skFitSpline(sketch, "E508", {"points": [v(-20.17, 39.1) * mm, v(-20.12, 39.13) * mm, v(-20.07, 39.3) * mm, v(-20.07, 39.47) * mm]});
            skFitSpline(sketch, "E509", {"points": [v(-20.07, 39.47) * mm, v(-20.07, 39.63) * mm, v(-20.02, 39.8) * mm, v(-19.96, 39.83) * mm]});
            skFitSpline(sketch, "E510", {"points": [v(-19.96, 39.83) * mm, v(-19.9, 39.87) * mm, v(-19.86, 39.98) * mm, v(-19.86, 40.08) * mm]});
            skFitSpline(sketch, "E511", {"points": [v(-19.86, 40.08) * mm, v(-19.86, 40.27) * mm, v(-19.4, 41.17) * mm, v(-19.07, 41.63) * mm]});
            skFitSpline(sketch, "E512", {"points": [v(-19.07, 41.63) * mm, v(-18.7, 42.16) * mm, v(-18, 42.8) * mm, v(-17.54, 43.04) * mm]});
            skFitSpline(sketch, "E513", {"points": [v(-17.54, 43.04) * mm, v(-17.4, 43.11) * mm, v(-17.26, 43.21) * mm, v(-17.22, 43.26) * mm]});
            skFitSpline(sketch, "E514", {"points": [v(-17.22, 43.26) * mm, v(-17.14, 43.4) * mm, v(-15.78, 43.5) * mm, v(-15.33, 43.42) * mm]});
            skFitSpline(sketch, "E515", {"points": [v(-15.33, 43.42) * mm, v(-14.6, 43.28) * mm, v(-14.08, 42.6) * mm, v(-14.08, 41.76) * mm]});
            skFitSpline(sketch, "E516", {"points": [v(-14.08, 41.76) * mm, v(-14.08, 41.24) * mm, v(-14.14, 41) * mm, v(-14.43, 40.3) * mm]});
            skFitSpline(sketch, "E517", {"points": [v(-14.43, 40.3) * mm, v(-14.5, 40.13) * mm, v(-14.82, 39.63) * mm, v(-15.25, 38.98) * mm]});
            skFitSpline(sketch, "E518", {"points": [v(-15.25, 38.98) * mm, v(-15.55, 38.54) * mm, v(-16.74, 37.38) * mm, v(-17.4, 36.88) * mm]});
            skFitSpline(sketch, "E519", {"points": [v(-17.4, 36.88) * mm, v(-17.63, 36.72) * mm, v(-17.83, 36.54) * mm, v(-17.85, 36.5) * mm]});
            skFitSpline(sketch, "E520", {"points": [v(-17.85, 36.5) * mm, v(-17.87, 36.46) * mm, v(-17.95, 36.42) * mm, v(-18.03, 36.42) * mm]});
            skFitSpline(sketch, "E521", {"points": [v(-18.03, 36.42) * mm, v(-18.27, 36.42) * mm, v(-18.2, 36.14) * mm, v(-17.9, 35.9) * mm]});
            skFitSpline(sketch, "E522", {"points": [v(-17.9, 35.9) * mm, v(-17.7, 35.74) * mm, v(-17.47, 35.69) * mm, v(-17, 35.69) * mm]});
            skFitSpline(sketch, "E523", {"points": [v(-17, 35.69) * mm, v(-16.67, 35.69) * mm, v(-16.3, 35.73) * mm, v(-16.18, 35.8) * mm]});
            skFitSpline(sketch, "E524", {"points": [v(-16.18, 35.8) * mm, v(-16.07, 35.85) * mm, v(-15.9, 35.94) * mm, v(-15.8, 35.98) * mm]});
            skFitSpline(sketch, "E525", {"points": [v(-15.8, 35.98) * mm, v(-15.2, 36.26) * mm, v(-14.79, 36.55) * mm, v(-14.04, 37.2) * mm]});
            skFitSpline(sketch, "E526", {"points": [v(-14.04, 37.2) * mm, v(-13.58, 37.6) * mm, v(-13.2, 37.88) * mm, v(-13.18, 37.83) * mm]});
            skFitSpline(sketch, "E527", {"points": [v(-13.18, 37.83) * mm, v(-13.17, 37.78) * mm, v(-13.1, 37.47) * mm, v(-13.03, 37.15) * mm]});
            skFitSpline(sketch, "E528", {"points": [v(-13.5, 36) * mm, v(-13.83, 35.68) * mm, v(-14.16, 35.4) * mm, v(-14.22, 35.38) * mm]});
            skFitSpline(sketch, "E529", {"points": [v(-14.22, 35.38) * mm, v(-14.28, 35.36) * mm, v(-14.43, 35.25) * mm, v(-14.55, 35.15) * mm]});
            skFitSpline(sketch, "E530", {"points": [v(-14.55, 35.15) * mm, v(-14.66, 35.04) * mm, v(-14.82, 34.95) * mm, v(-14.9, 34.95) * mm]});
            skFitSpline(sketch, "E531", {"points": [v(-14.9, 34.95) * mm, v(-14.97, 34.95) * mm, v(-15.03, 34.9) * mm, v(-15.03, 34.85) * mm]});
            skFitSpline(sketch, "E532", {"points": [v(-15.03, 34.85) * mm, v(-15.03, 34.8) * mm, v(-15.17, 34.73) * mm, v(-15.34, 34.69) * mm]});
            skFitSpline(sketch, "E533", {"points": [v(-15.34, 34.69) * mm, v(-15.52, 34.65) * mm, v(-15.68, 34.58) * mm, v(-15.72, 34.52) * mm]});
            skFitSpline(sketch, "E534", {"points": [v(-15.72, 34.52) * mm, v(-15.75, 34.47) * mm, v(-15.94, 34.43) * mm, v(-16.13, 34.43) * mm]});
            skFitSpline(sketch, "E535", {"points": [v(-16.13, 34.43) * mm, v(-16.33, 34.43) * mm, v(-16.52, 34.38) * mm, v(-16.55, 34.32) * mm]});
            skFitSpline(sketch, "E536", {"points": [v(-16.55, 34.32) * mm, v(-16.59, 34.26) * mm, v(-16.87, 34.22) * mm, v(-17.18, 34.22) * mm]});
            skFitSpline(sketch, "E537", {"points": [v(-17.18, 34.22) * mm, v(-17.5, 34.22) * mm, v(-17.78, 34.26) * mm, v(-17.81, 34.32) * mm]});
            skLineSegment(sketch, "E538", {"start": v(-13.03, 37.15) * mm, "end": v(-12.9, 36.56) * mm});
            skLineSegment(sketch, "E539", {"start": v(-12.9, 36.56) * mm, "end": v(-13.5, 36) * mm});
            skLineSegment(sketch, "E540", {"start": v(-13.5, 36) * mm, "end": v(-13.03, 37.15) * mm});
            skFitSpline(sketch, "E541", {"points": [v(-17.96, 38.2) * mm, v(-17.13, 38.9) * mm, v(-16.1, 40.16) * mm, v(-15.77, 40.88) * mm]});
            skFitSpline(sketch, "E542", {"points": [v(-15.77, 40.88) * mm, v(-15.64, 41.17) * mm, v(-15.49, 41.49) * mm, v(-15.44, 41.59) * mm]});
            skFitSpline(sketch, "E543", {"points": [v(-15.44, 41.59) * mm, v(-15.3, 41.87) * mm, v(-15.33, 42.15) * mm, v(-15.52, 42.31) * mm]});
            skFitSpline(sketch, "E544", {"points": [v(-15.52, 42.31) * mm, v(-15.65, 42.43) * mm, v(-15.7, 42.43) * mm, v(-15.74, 42.33) * mm]});
            skFitSpline(sketch, "E545", {"points": [v(-15.74, 42.33) * mm, v(-15.76, 42.25) * mm, v(-15.87, 42.2) * mm, v(-15.97, 42.2) * mm]});
            skFitSpline(sketch, "E546", {"points": [v(-15.97, 42.2) * mm, v(-16.48, 42.2) * mm, v(-17.59, 41.4) * mm, v(-17.92, 40.81) * mm]});
            skFitSpline(sketch, "E547", {"points": [v(-17.92, 40.81) * mm, v(-18.49, 39.8) * mm, v(-18.8, 38.94) * mm, v(-18.81, 38.31) * mm]});
            skFitSpline(sketch, "E548", {"points": [v(-18.81, 38.31) * mm, v(-18.84, 37.4) * mm, v(-18.9, 37.4) * mm, v(-17.96, 38.2) * mm]});
            skFitSpline(sketch, "E549", {"points": [v(13.42, 35.44) * mm, v(12.72, 35.52) * mm, v(12.05, 35.98) * mm, v(12.05, 36.38) * mm]});
            skFitSpline(sketch, "E550", {"points": [v(12.05, 36.38) * mm, v(12.05, 36.67) * mm, v(12.79, 38.03) * mm, v(13.1, 38.31) * mm]});
            skFitSpline(sketch, "E551", {"points": [v(13.1, 38.31) * mm, v(13.19, 38.4) * mm, v(13.4, 38.76) * mm, v(13.51, 39) * mm]});
            skFitSpline(sketch, "E552", {"points": [v(13.51, 39) * mm, v(13.56, 39.12) * mm, v(13.68, 39.27) * mm, v(13.77, 39.35) * mm]});
            skFitSpline(sketch, "E553", {"points": [v(13.77, 39.35) * mm, v(13.87, 39.43) * mm, v(13.94, 39.54) * mm, v(13.94, 39.6) * mm]});
            skFitSpline(sketch, "E554", {"points": [v(13.94, 39.6) * mm, v(13.94, 39.64) * mm, v(14.06, 39.84) * mm, v(14.2, 40.03) * mm]});
            skFitSpline(sketch, "E555", {"points": [v(14.2, 40.03) * mm, v(14.35, 40.22) * mm, v(14.47, 40.42) * mm, v(14.47, 40.48) * mm]});
            skFitSpline(sketch, "E556", {"points": [v(14.47, 40.48) * mm, v(14.47, 40.54) * mm, v(14.56, 40.67) * mm, v(14.68, 40.78) * mm]});
            skFitSpline(sketch, "E557", {"points": [v(14.68, 40.78) * mm, v(14.8, 40.88) * mm, v(14.89, 41.02) * mm, v(14.89, 41.1) * mm]});
            skFitSpline(sketch, "E558", {"points": [v(14.89, 41.1) * mm, v(14.89, 41.16) * mm, v(14.98, 41.3) * mm, v(15.1, 41.4) * mm]});
            skFitSpline(sketch, "E559", {"points": [v(15.1, 41.4) * mm, v(15.21, 41.51) * mm, v(15.3, 41.65) * mm, v(15.3, 41.7) * mm]});
            skFitSpline(sketch, "E560", {"points": [v(15.3, 41.7) * mm, v(15.3, 41.76) * mm, v(15.37, 41.89) * mm, v(15.45, 41.98) * mm]});
            skFitSpline(sketch, "E561", {"points": [v(15.45, 41.98) * mm, v(15.7, 42.26) * mm, v(16.04, 42.93) * mm, v(16.04, 43.14) * mm]});
            skFitSpline(sketch, "E562", {"points": [v(16.04, 43.14) * mm, v(16.04, 43.36) * mm, v(16.4, 43.44) * mm, v(16.52, 43.24) * mm]});
            skFitSpline(sketch, "E563", {"points": [v(16.52, 43.24) * mm, v(16.55, 43.19) * mm, v(16.66, 43.14) * mm, v(16.76, 43.14) * mm]});
            skFitSpline(sketch, "E564", {"points": [v(16.76, 43.14) * mm, v(17.08, 43.14) * mm, v(17.51, 42.88) * mm, v(17.51, 42.7) * mm]});
            skFitSpline(sketch, "E565", {"points": [v(17.51, 42.7) * mm, v(17.51, 42.51) * mm, v(17.32, 42.1) * mm, v(17.19, 41.98) * mm]});
            skFitSpline(sketch, "E566", {"points": [v(17.19, 41.98) * mm, v(17.15, 41.96) * mm, v(17.08, 41.81) * mm, v(17.04, 41.67) * mm]});
            skFitSpline(sketch, "E567", {"points": [v(17.04, 41.67) * mm, v(16.95, 41.39) * mm, v(16.57, 40.8) * mm, v(16.44, 40.74) * mm]});
            skFitSpline(sketch, "E568", {"points": [v(16.44, 40.74) * mm, v(16.4, 40.72) * mm, v(16.36, 40.66) * mm, v(16.36, 40.61) * mm]});
            skFitSpline(sketch, "E569", {"points": [v(16.36, 40.61) * mm, v(16.36, 40.56) * mm, v(16.2, 40.29) * mm, v(16, 40) * mm]});
            skFitSpline(sketch, "E570", {"points": [v(16, 40) * mm, v(15.79, 39.72) * mm, v(15.62, 39.47) * mm, v(15.62, 39.43) * mm]});
            skFitSpline(sketch, "E571", {"points": [v(15.62, 39.43) * mm, v(15.62, 39.4) * mm, v(15.41, 39.07) * mm, v(15.15, 38.7) * mm]});
            skFitSpline(sketch, "E572", {"points": [v(15.15, 38.7) * mm, v(14.9, 38.32) * mm, v(14.68, 37.97) * mm, v(14.68, 37.92) * mm]});
            skFitSpline(sketch, "E573", {"points": [v(14.68, 37.92) * mm, v(14.68, 37.86) * mm, v(14.58, 37.73) * mm, v(14.47, 37.63) * mm]});
            skFitSpline(sketch, "E574", {"points": [v(14.47, 37.63) * mm, v(14.35, 37.52) * mm, v(14.26, 37.38) * mm, v(14.26, 37.3) * mm]});
            skFitSpline(sketch, "E575", {"points": [v(14.26, 37.3) * mm, v(14.26, 37.23) * mm, v(14.2, 37.13) * mm, v(14.13, 37.08) * mm]});
            skFitSpline(sketch, "E576", {"points": [v(14.13, 37.08) * mm, v(13.95, 36.97) * mm, v(13.73, 36.56) * mm, v(13.8, 36.48) * mm]});
            skFitSpline(sketch, "E577", {"points": [v(13.8, 36.48) * mm, v(13.84, 36.45) * mm, v(14.05, 36.42) * mm, v(14.28, 36.42) * mm]});
            skFitSpline(sketch, "E578", {"points": [v(14.28, 36.42) * mm, v(14.73, 36.42) * mm, v(14.8, 36.25) * mm, v(14.47, 35.95) * mm]});
            skFitSpline(sketch, "E579", {"points": [v(14.47, 35.95) * mm, v(14.36, 35.85) * mm, v(14.24, 35.68) * mm, v(14.2, 35.57) * mm]});
            skFitSpline(sketch, "E580", {"points": [v(14.2, 35.57) * mm, v(14.17, 35.46) * mm, v(14.06, 35.38) * mm, v(13.96, 35.39) * mm]});
            skFitSpline(sketch, "E581", {"points": [v(13.96, 35.39) * mm, v(13.87, 35.4) * mm, v(13.62, 35.42) * mm, v(13.42, 35.44) * mm]});
            skFitSpline(sketch, "E582", {"points": [v(5.23, 35.74) * mm, v(5.23, 35.89) * mm, v(5.17, 36.1) * mm, v(5.1, 36.21) * mm]});
            skFitSpline(sketch, "E583", {"points": [v(5.1, 36.21) * mm, v(4.85, 36.6) * mm, v(5.1, 36.78) * mm, v(6.03, 36.85) * mm]});
            skFitSpline(sketch, "E584", {"points": [v(6.03, 36.85) * mm, v(6.94, 36.92) * mm, v(7.18, 37.02) * mm, v(7.78, 37.58) * mm]});
            skFitSpline(sketch, "E585", {"points": [v(7.78, 37.58) * mm, v(8.19, 37.95) * mm, v(8.8, 39.03) * mm, v(8.8, 39.38) * mm]});
            skFitSpline(sketch, "E586", {"points": [v(8.8, 39.38) * mm, v(8.8, 39.48) * mm, v(8.85, 39.57) * mm, v(8.9, 39.57) * mm]});
            skFitSpline(sketch, "E587", {"points": [v(8.9, 39.57) * mm, v(8.96, 39.57) * mm, v(9, 39.64) * mm, v(9, 39.73) * mm]});
            skFitSpline(sketch, "E588", {"points": [v(9, 39.73) * mm, v(9, 39.82) * mm, v(9.05, 39.97) * mm, v(9.1, 40.07) * mm]});
            skFitSpline(sketch, "E589", {"points": [v(9.1, 40.07) * mm, v(9.15, 40.17) * mm, v(9.24, 40.37) * mm, v(9.3, 40.52) * mm]});
            skFitSpline(sketch, "E590", {"points": [v(9.3, 40.52) * mm, v(9.36, 40.66) * mm, v(9.48, 40.95) * mm, v(9.58, 41.16) * mm]});
            skFitSpline(sketch, "E591", {"points": [v(9.58, 41.16) * mm, v(9.67, 41.37) * mm, v(9.74, 41.64) * mm, v(9.74, 41.76) * mm]});
            skFitSpline(sketch, "E592", {"points": [v(9.74, 41.76) * mm, v(9.74, 41.89) * mm, v(9.8, 41.98) * mm, v(9.85, 41.98) * mm]});
            skFitSpline(sketch, "E593", {"points": [v(9.85, 41.98) * mm, v(9.9, 41.98) * mm, v(9.95, 42.08) * mm, v(9.95, 42.19) * mm]});
            skFitSpline(sketch, "E594", {"points": [v(9.95, 42.19) * mm, v(9.95, 42.3) * mm, v(10.01, 42.4) * mm, v(10.08, 42.43) * mm]});
            skFitSpline(sketch, "E595", {"points": [v(10.08, 42.43) * mm, v(10.15, 42.45) * mm, v(10.17, 42.54) * mm, v(10.14, 42.63) * mm]});
            skFitSpline(sketch, "E596", {"points": [v(10.14, 42.63) * mm, v(10.08, 42.8) * mm, v(9.16, 42.93) * mm, v(6.86, 43.12) * mm]});
            skFitSpline(sketch, "E597", {"points": [v(6.86, 43.12) * mm, v(6.1, 43.19) * mm, v(6.01, 43.21) * mm, v(5.98, 43.43) * mm]});
            skFitSpline(sketch, "E598", {"points": [v(5.98, 43.43) * mm, v(5.97, 43.56) * mm, v(6, 43.66) * mm, v(6.06, 43.66) * mm]});
            skFitSpline(sketch, "E599", {"points": [v(6.06, 43.66) * mm, v(6.12, 43.66) * mm, v(6.18, 43.75) * mm, v(6.18, 43.85) * mm]});
            skFitSpline(sketch, "E600", {"points": [v(6.18, 43.85) * mm, v(6.18, 43.95) * mm, v(6.25, 44.12) * mm, v(6.33, 44.23) * mm]});
            skFitSpline(sketch, "E601", {"points": [v(6.33, 44.23) * mm, v(6.46, 44.4) * mm, v(6.56, 44.42) * mm, v(6.98, 44.36) * mm]});
            skFitSpline(sketch, "E602", {"points": [v(6.98, 44.36) * mm, v(7.26, 44.32) * mm, v(7.75, 44.27) * mm, v(8.06, 44.25) * mm]});
            skFitSpline(sketch, "E603", {"points": [v(8.06, 44.25) * mm, v(9.37, 44.15) * mm, v(10.12, 44.05) * mm, v(10.24, 43.96) * mm]});
            skFitSpline(sketch, "E604", {"points": [v(10.24, 43.96) * mm, v(10.43, 43.8) * mm, v(10.69, 43.94) * mm, v(10.69, 44.19) * mm]});
            skFitSpline(sketch, "E605", {"points": [v(10.69, 44.19) * mm, v(10.69, 44.3) * mm, v(10.74, 44.4) * mm, v(10.8, 44.4) * mm]});
            skFitSpline(sketch, "E606", {"points": [v(10.8, 44.4) * mm, v(10.85, 44.4) * mm, v(10.9, 44.48) * mm, v(10.9, 44.58) * mm]});
            skFitSpline(sketch, "E607", {"points": [v(10.9, 44.58) * mm, v(10.9, 44.68) * mm, v(11.15, 45.27) * mm, v(11.46, 45.9) * mm]});
            skFitSpline(sketch, "E608", {"points": [v(11.46, 45.9) * mm, v(12.08, 47.15) * mm, v(12.1, 47.1) * mm, v(11.1, 47.25) * mm]});
            skFitSpline(sketch, "E609", {"points": [v(11.1, 47.25) * mm, v(9.72, 47.48) * mm, v(9.07, 47.56) * mm, v(7.6, 47.68) * mm]});
            skFitSpline(sketch, "E610", {"points": [v(7.6, 47.68) * mm, v(6.7, 47.75) * mm, v(6.02, 47.86) * mm, v(6.02, 47.92) * mm]});
            skFitSpline(sketch, "E611", {"points": [v(6.02, 47.92) * mm, v(6.02, 47.97) * mm, v(6.12, 48.22) * mm, v(6.23, 48.47) * mm]});
            skFitSpline(sketch, "E612", {"points": [v(7.64, 48.87) * mm, v(8.93, 48.82) * mm, v(10.2, 48.68) * mm, v(11.06, 48.5) * mm]});
            skFitSpline(sketch, "E613", {"points": [v(11.06, 48.5) * mm, v(11.35, 48.44) * mm, v(11.94, 48.33) * mm, v(12.39, 48.26) * mm]});
            skFitSpline(sketch, "E614", {"points": [v(12.39, 48.26) * mm, v(12.83, 48.19) * mm, v(13.23, 48.1) * mm, v(13.27, 48.05) * mm]});
            skFitSpline(sketch, "E615", {"points": [v(13.27, 48.05) * mm, v(13.31, 48) * mm, v(13.52, 47.97) * mm, v(13.72, 47.96) * mm]});
            skFitSpline(sketch, "E616", {"points": [v(13.72, 47.96) * mm, v(13.93, 47.96) * mm, v(14.18, 47.9) * mm, v(14.28, 47.83) * mm]});
            skFitSpline(sketch, "E617", {"points": [v(14.28, 47.83) * mm, v(14.43, 47.7) * mm, v(14.4, 47.64) * mm, v(13.92, 47.18) * mm]});
            skFitSpline(sketch, "E618", {"points": [v(13.92, 47.18) * mm, v(13.56, 46.83) * mm, v(13.27, 46.4) * mm, v(13, 45.82) * mm]});
            skFitSpline(sketch, "E619", {"points": [v(13, 45.82) * mm, v(12.05, 43.8) * mm, v(12.03, 43.73) * mm, v(12.48, 43.57) * mm]});
            skFitSpline(sketch, "E620", {"points": [v(12.48, 43.57) * mm, v(12.67, 43.5) * mm, v(12.9, 43.45) * mm, v(13.01, 43.45) * mm]});
            skFitSpline(sketch, "E621", {"points": [v(13.01, 43.45) * mm, v(13.25, 43.45) * mm, v(13.25, 43.48) * mm, v(13, 42.95) * mm]});
            skFitSpline(sketch, "E622", {"points": [v(13, 42.95) * mm, v(12.88, 42.72) * mm, v(12.79, 42.45) * mm, v(12.79, 42.36) * mm]});
            skFitSpline(sketch, "E623", {"points": [v(12.79, 42.36) * mm, v(12.79, 42.18) * mm, v(12.58, 42.14) * mm, v(12.42, 42.29) * mm]});
            skFitSpline(sketch, "E624", {"points": [v(12.42, 42.29) * mm, v(12.36, 42.34) * mm, v(12.17, 42.4) * mm, v(12, 42.44) * mm]});
            skFitSpline(sketch, "E625", {"points": [v(12, 42.44) * mm, v(11.63, 42.5) * mm, v(11.5, 42.36) * mm, v(11.37, 41.77) * mm]});
            skFitSpline(sketch, "E626", {"points": [v(11.37, 41.77) * mm, v(11.33, 41.58) * mm, v(11.26, 41.34) * mm, v(11.21, 41.25) * mm]});
            skFitSpline(sketch, "E627", {"points": [v(11.21, 41.25) * mm, v(11.17, 41.16) * mm, v(11.03, 40.89) * mm, v(10.91, 40.64) * mm]});
            skFitSpline(sketch, "E628", {"points": [v(10.91, 40.64) * mm, v(10.79, 40.39) * mm, v(10.69, 40.1) * mm, v(10.69, 39.99) * mm]});
            skFitSpline(sketch, "E629", {"points": [v(10.69, 39.99) * mm, v(10.69, 39.88) * mm, v(10.64, 39.76) * mm, v(10.58, 39.73) * mm]});
            skFitSpline(sketch, "E630", {"points": [v(10.58, 39.73) * mm, v(10.53, 39.7) * mm, v(10.48, 39.6) * mm, v(10.48, 39.51) * mm]});
            skFitSpline(sketch, "E631", {"points": [v(10.48, 39.51) * mm, v(10.48, 39.3) * mm, v(10.13, 38.52) * mm, v(10.03, 38.52) * mm]});
            skFitSpline(sketch, "E632", {"points": [v(10.03, 38.52) * mm, v(10, 38.52) * mm, v(9.95, 38.43) * mm, v(9.95, 38.31) * mm]});
            skFitSpline(sketch, "E633", {"points": [v(9.95, 38.31) * mm, v(9.95, 38.2) * mm, v(9.92, 38.1) * mm, v(9.87, 38.1) * mm]});
            skFitSpline(sketch, "E634", {"points": [v(9.87, 38.1) * mm, v(9.82, 38.1) * mm, v(9.72, 37.94) * mm, v(9.64, 37.74) * mm]});
            skFitSpline(sketch, "E635", {"points": [v(9.64, 37.74) * mm, v(9.35, 37) * mm, v(7.7, 35.69) * mm, v(7.07, 35.69) * mm]});
            skFitSpline(sketch, "E636", {"points": [v(7.07, 35.69) * mm, v(6.93, 35.69) * mm, v(6.79, 35.64) * mm, v(6.75, 35.58) * mm]});
            skFitSpline(sketch, "E637", {"points": [v(6.75, 35.58) * mm, v(6.72, 35.52) * mm, v(6.36, 35.48) * mm, v(5.96, 35.48) * mm]});
            skFitSpline(sketch, "E638", {"points": [v(5.96, 35.48) * mm, v(5.25, 35.48) * mm, v(5.23, 35.48) * mm, v(5.23, 35.74) * mm]});
            skLineSegment(sketch, "E639", {"start": v(6.23, 48.47) * mm, "end": v(6.44, 48.92) * mm});
            skLineSegment(sketch, "E640", {"start": v(6.44, 48.92) * mm, "end": v(7.64, 48.87) * mm});
            skLineSegment(sketch, "E641", {"start": v(7.64, 48.87) * mm, "end": v(6.23, 48.47) * mm});
            skFitSpline(sketch, "E642", {"points": [v(-12.37, 36.5) * mm, v(-12.44, 39.16) * mm, v(-12.62, 43.81) * mm, v(-12.67, 44.15) * mm]});
            skFitSpline(sketch, "E643", {"points": [v(-12.34, 44.64) * mm, v(-12.11, 44.68) * mm, v(-11.8, 44.73) * mm, v(-11.62, 44.77) * mm]});
            skFitSpline(sketch, "E644", {"points": [v(-11.62, 44.77) * mm, v(-11.3, 44.83) * mm, v(-11.3, 44.82) * mm, v(-11.17, 44.27) * mm]});
            skFitSpline(sketch, "E645", {"points": [v(-11.17, 44.27) * mm, v(-11.1, 43.96) * mm, v(-11.04, 43.54) * mm, v(-11.04, 43.33) * mm]});
            skFitSpline(sketch, "E646", {"points": [v(-11.04, 43.33) * mm, v(-11.04, 43.11) * mm, v(-11, 42.91) * mm, v(-10.94, 42.88) * mm]});
            skFitSpline(sketch, "E647", {"points": [v(-10.94, 42.88) * mm, v(-10.88, 42.84) * mm, v(-10.83, 42.89) * mm, v(-10.83, 42.98) * mm]});
            skFitSpline(sketch, "E648", {"points": [v(-10.83, 42.98) * mm, v(-10.83, 43.07) * mm, v(-10.79, 43.22) * mm, v(-10.73, 43.32) * mm]});
            skFitSpline(sketch, "E649", {"points": [v(-10.73, 43.32) * mm, v(-10.68, 43.42) * mm, v(-10.56, 43.7) * mm, v(-10.46, 43.93) * mm]});
            skFitSpline(sketch, "E650", {"points": [v(-10.46, 43.93) * mm, v(-10.36, 44.16) * mm, v(-10.25, 44.37) * mm, v(-10.21, 44.4) * mm]});
            skFitSpline(sketch, "E651", {"points": [v(-10.21, 44.4) * mm, v(-10.18, 44.43) * mm, v(-10.02, 44.62) * mm, v(-9.87, 44.82) * mm]});
            skFitSpline(sketch, "E652", {"points": [v(-9.87, 44.82) * mm, v(-9.72, 45.03) * mm, v(-9.4, 45.29) * mm, v(-9.16, 45.4) * mm]});
            skFitSpline(sketch, "E653", {"points": [v(-9.16, 45.4) * mm, v(-8.93, 45.51) * mm, v(-8.73, 45.64) * mm, v(-8.73, 45.68) * mm]});
            skFitSpline(sketch, "E654", {"points": [v(-8.73, 45.68) * mm, v(-8.73, 45.81) * mm, v(-7.85, 45.77) * mm, v(-7.55, 45.63) * mm]});
            skFitSpline(sketch, "E655", {"points": [v(-7.55, 45.63) * mm, v(-7.28, 45.51) * mm, v(-7.26, 45.46) * mm, v(-7.26, 44.83) * mm]});
            skLineSegment(sketch, "E656", {"start": v(-12.67, 44.15) * mm, "end": v(-12.74, 44.59) * mm});
            skLineSegment(sketch, "E657", {"start": v(-12.74, 44.59) * mm, "end": v(-12.34, 44.64) * mm});
            skLineSegment(sketch, "E658", {"start": v(-12.34, 44.64) * mm, "end": v(-12.67, 44.15) * mm});
            skFitSpline(sketch, "E659", {"points": [v(-7.6, 44.24) * mm, v(-8.33, 44.41) * mm, v(-8.67, 44.27) * mm, v(-8.98, 43.67) * mm]});
            skFitSpline(sketch, "E660", {"points": [v(-8.98, 43.67) * mm, v(-9.74, 42.21) * mm, v(-9.89, 41.9) * mm, v(-9.89, 41.65) * mm]});
            skFitSpline(sketch, "E661", {"points": [v(-9.89, 41.65) * mm, v(-9.89, 41.55) * mm, v(-9.93, 41.46) * mm, v(-10, 41.46) * mm]});
            skFitSpline(sketch, "E662", {"points": [v(-10, 41.46) * mm, v(-10.05, 41.46) * mm, v(-10.1, 41.36) * mm, v(-10.1, 41.25) * mm]});
            skFitSpline(sketch, "E663", {"points": [v(-10.1, 41.25) * mm, v(-10.1, 41.13) * mm, v(-10.14, 40.96) * mm, v(-10.19, 40.85) * mm]});
            skFitSpline(sketch, "E664", {"points": [v(-10.19, 40.85) * mm, v(-10.36, 40.52) * mm, v(-10.51, 39.94) * mm, v(-10.58, 39.4) * mm]});
            skFitSpline(sketch, "E665", {"points": [v(-10.58, 39.4) * mm, v(-10.6, 39.12) * mm, v(-10.68, 38.8) * mm, v(-10.73, 38.68) * mm]});
            skFitSpline(sketch, "E666", {"points": [v(-10.73, 38.68) * mm, v(-10.78, 38.56) * mm, v(-10.84, 38.18) * mm, v(-10.87, 37.84) * mm]});
            skFitSpline(sketch, "E667", {"points": [v(-10.87, 37.84) * mm, v(-10.9, 37.5) * mm, v(-10.96, 37.02) * mm, v(-11, 36.8) * mm]});
            skFitSpline(sketch, "E668", {"points": [v(-11, 36.8) * mm, v(-11.09, 36.42) * mm, v(-11.13, 36.38) * mm, v(-11.62, 36.25) * mm]});
            skFitSpline(sketch, "E669", {"points": [v(-11.62, 36.25) * mm, v(-12.35, 36.06) * mm, v(-12.36, 36.06) * mm, v(-12.37, 36.5) * mm]});
            skLineSegment(sketch, "E670", {"start": v(-7.26, 44.83) * mm, "end": v(-7.26, 44.16) * mm});
            skLineSegment(sketch, "E671", {"start": v(-7.26, 44.16) * mm, "end": v(-7.6, 44.24) * mm});
            skLineSegment(sketch, "E672", {"start": v(-7.6, 44.24) * mm, "end": v(-7.26, 44.83) * mm});
            skFitSpline(sketch, "E673", {"points": [v(30.02, 37.08) * mm, v(29.77, 37.36) * mm, v(29.73, 37.68) * mm, v(29.93, 38.02) * mm]});
            skFitSpline(sketch, "E674", {"points": [v(29.93, 38.02) * mm, v(30.19, 38.49) * mm, v(30.43, 38.63) * mm, v(31, 38.63) * mm]});
            skFitSpline(sketch, "E675", {"points": [v(31, 38.63) * mm, v(31.47, 38.63) * mm, v(31.58, 38.59) * mm, v(31.72, 38.37) * mm]});
            skFitSpline(sketch, "E676", {"points": [v(31.72, 38.37) * mm, v(31.98, 37.98) * mm, v(31.93, 37.62) * mm, v(31.57, 37.21) * mm]});
            skFitSpline(sketch, "E677", {"points": [v(31.57, 37.21) * mm, v(31.28, 36.89) * mm, v(31.18, 36.84) * mm, v(30.75, 36.84) * mm]});
            skFitSpline(sketch, "E678", {"points": [v(30.75, 36.84) * mm, v(30.36, 36.84) * mm, v(30.2, 36.9) * mm, v(30.02, 37.08) * mm]});
            skFitSpline(sketch, "E679", {"points": [v(-7.05, 37.92) * mm, v(-7.05, 38.11) * mm, v(-7, 38.31) * mm, v(-6.96, 38.37) * mm]});
            skFitSpline(sketch, "E680", {"points": [v(-6.96, 38.37) * mm, v(-6.9, 38.42) * mm, v(-6.83, 38.7) * mm, v(-6.8, 39) * mm]});
            skFitSpline(sketch, "E681", {"points": [v(-6.8, 39) * mm, v(-6.72, 39.78) * mm, v(-6.43, 41.85) * mm, v(-6.3, 42.56) * mm]});
            skFitSpline(sketch, "E682", {"points": [v(-6.3, 42.56) * mm, v(-6.25, 42.9) * mm, v(-6.18, 43.43) * mm, v(-6.14, 43.72) * mm]});
            skFitSpline(sketch, "E683", {"points": [v(-6.14, 43.72) * mm, v(-6.11, 44) * mm, v(-6.04, 44.29) * mm, v(-6, 44.34) * mm]});
            skFitSpline(sketch, "E684", {"points": [v(-6, 44.34) * mm, v(-5.87, 44.47) * mm, v(-5.87, 45.41) * mm, v(-6, 45.65) * mm]});
            skFitSpline(sketch, "E685", {"points": [v(-6, 45.65) * mm, v(-6.09, 45.82) * mm, v(-6.03, 45.84) * mm, v(-5.34, 45.9) * mm]});
            skFitSpline(sketch, "E686", {"points": [v(-5.34, 45.9) * mm, v(-4.93, 45.94) * mm, v(-4.55, 45.93) * mm, v(-4.5, 45.88) * mm]});
            skFitSpline(sketch, "E687", {"points": [v(-4.5, 45.88) * mm, v(-4.38, 45.76) * mm, v(-4.47, 44.18) * mm, v(-4.63, 43.5) * mm]});
            skFitSpline(sketch, "E688", {"points": [v(-4.63, 43.5) * mm, v(-4.95, 42.13) * mm, v(-4.86, 41.9) * mm, v(-4.32, 42.74) * mm]});
            skFitSpline(sketch, "E689", {"points": [v(-4.32, 42.74) * mm, v(-4.12, 43.04) * mm, v(-3.76, 43.49) * mm, v(-3.51, 43.73) * mm]});
            skFitSpline(sketch, "E690", {"points": [v(-3.51, 43.73) * mm, v(-3.27, 43.98) * mm, v(-3.06, 44.2) * mm, v(-3.06, 44.24) * mm]});
            skFitSpline(sketch, "E691", {"points": [v(-3.06, 44.24) * mm, v(-3.06, 44.34) * mm, v(-2.78, 44.6) * mm, v(-2.67, 44.6) * mm]});
            skFitSpline(sketch, "E692", {"points": [v(-2.67, 44.6) * mm, v(-2.62, 44.6) * mm, v(-2.44, 44.76) * mm, v(-2.27, 44.94) * mm]});
            skFitSpline(sketch, "E693", {"points": [v(-2.27, 44.94) * mm, v(-1.9, 45.33) * mm, v(-0.9, 46.08) * mm, v(-0.76, 46.08) * mm]});
            skFitSpline(sketch, "E694", {"points": [v(-0.76, 46.08) * mm, v(-0.7, 46.08) * mm, v(-0.65, 46.13) * mm, v(-0.65, 46.18) * mm]});
            skFitSpline(sketch, "E695", {"points": [v(-0.65, 46.18) * mm, v(-0.65, 46.24) * mm, v(-0.56, 46.29) * mm, v(-0.44, 46.29) * mm]});
            skFitSpline(sketch, "E696", {"points": [v(-0.44, 46.29) * mm, v(-0.33, 46.29) * mm, v(-0.21, 46.34) * mm, v(-0.18, 46.4) * mm]});
            skFitSpline(sketch, "E697", {"points": [v(-0.18, 46.4) * mm, v(-0.05, 46.6) * mm, v(0.28, 46.49) * mm, v(0.75, 46.07) * mm]});
            skFitSpline(sketch, "E698", {"points": [v(0.75, 46.07) * mm, v(1.2, 45.68) * mm, v(1.24, 45.6) * mm, v(1.24, 45.18) * mm]});
            skFitSpline(sketch, "E699", {"points": [v(1.24, 45.18) * mm, v(1.24, 44.92) * mm, v(1.2, 44.63) * mm, v(1.15, 44.53) * mm]});
            skFitSpline(sketch, "E700", {"points": [v(1.15, 44.53) * mm, v(1.1, 44.43) * mm, v(1, 44.02) * mm, v(0.93, 43.61) * mm]});
            skFitSpline(sketch, "E701", {"points": [v(0.93, 43.61) * mm, v(0.86, 43.2) * mm, v(0.76, 42.66) * mm, v(0.7, 42.4) * mm]});
            skFitSpline(sketch, "E702", {"points": [v(0.7, 42.4) * mm, v(0.64, 42.14) * mm, v(0.57, 41.74) * mm, v(0.54, 41.51) * mm]});
            skFitSpline(sketch, "E703", {"points": [v(0.54, 41.51) * mm, v(0.51, 41.28) * mm, v(0.44, 41.05) * mm, v(0.4, 41) * mm]});
            skFitSpline(sketch, "E704", {"points": [v(0.4, 41) * mm, v(0.34, 40.94) * mm, v(0.3, 40.72) * mm, v(0.3, 40.52) * mm]});
            skFitSpline(sketch, "E705", {"points": [v(0.3, 40.52) * mm, v(0.3, 40.3) * mm, v(0.26, 40.1) * mm, v(0.2, 40.04) * mm]});
            skFitSpline(sketch, "E706", {"points": [v(0.2, 40.04) * mm, v(0.07, 39.89) * mm, v(-0.02, 39.16) * mm, v(0.09, 39.1) * mm]});
            skFitSpline(sketch, "E707", {"points": [v(0.09, 39.1) * mm, v(0.14, 39.06) * mm, v(0.27, 39.1) * mm, v(0.38, 39.16) * mm]});
            skFitSpline(sketch, "E708", {"points": [v(0.38, 39.16) * mm, v(0.74, 39.39) * mm, v(0.92, 39.22) * mm, v(0.86, 38.7) * mm]});
            skFitSpline(sketch, "E709", {"points": [v(0.86, 38.7) * mm, v(0.83, 38.46) * mm, v(0.75, 38.2) * mm, v(0.67, 38.11) * mm]});
            skFitSpline(sketch, "E710", {"points": [v(0.67, 38.11) * mm, v(0.51, 37.96) * mm, v(-0.18, 37.8) * mm, v(-0.73, 37.8) * mm]});
            skFitSpline(sketch, "E711", {"points": [v(-0.73, 37.8) * mm, v(-1.23, 37.78) * mm, v(-1.6, 38.2) * mm, v(-1.6, 38.8) * mm]});
            skFitSpline(sketch, "E712", {"points": [v(-1.6, 38.8) * mm, v(-1.6, 39.04) * mm, v(-1.55, 39.27) * mm, v(-1.49, 39.3) * mm]});
            skFitSpline(sketch, "E713", {"points": [v(-1.49, 39.3) * mm, v(-1.43, 39.34) * mm, v(-1.38, 39.58) * mm, v(-1.38, 39.83) * mm]});
            skFitSpline(sketch, "E714", {"points": [v(-1.38, 39.83) * mm, v(-1.38, 40.09) * mm, v(-1.34, 40.32) * mm, v(-1.29, 40.35) * mm]});
            skFitSpline(sketch, "E715", {"points": [v(-1.29, 40.35) * mm, v(-1.24, 40.38) * mm, v(-1.17, 40.59) * mm, v(-1.14, 40.8) * mm]});
            skFitSpline(sketch, "E716", {"points": [v(-1.14, 40.8) * mm, v(-1.1, 41.02) * mm, v(-1, 41.6) * mm, v(-0.91, 42.09) * mm]});
            skFitSpline(sketch, "E717", {"points": [v(-0.91, 42.09) * mm, v(-0.82, 42.58) * mm, v(-0.72, 43.17) * mm, v(-0.68, 43.4) * mm]});
            skFitSpline(sketch, "E718", {"points": [v(-0.68, 43.4) * mm, v(-0.65, 43.63) * mm, v(-0.58, 43.87) * mm, v(-0.53, 43.92) * mm]});
            skFitSpline(sketch, "E719", {"points": [v(-0.53, 43.92) * mm, v(-0.43, 44.03) * mm, v(-0.4, 44.6) * mm, v(-0.5, 44.6) * mm]});
            skFitSpline(sketch, "E720", {"points": [v(-0.5, 44.6) * mm, v(-0.69, 44.6) * mm, v(-2.33, 43.13) * mm, v(-2.33, 42.96) * mm]});
            skFitSpline(sketch, "E721", {"points": [v(-2.33, 42.96) * mm, v(-2.33, 42.93) * mm, v(-2.55, 42.65) * mm, v(-2.83, 42.36) * mm]});
            skFitSpline(sketch, "E722", {"points": [v(-2.83, 42.36) * mm, v(-3.41, 41.72) * mm, v(-3.54, 41.56) * mm, v(-3.93, 40.96) * mm]});
            skFitSpline(sketch, "E723", {"points": [v(-3.93, 40.96) * mm, v(-4.52, 40.05) * mm, v(-5.37, 38.45) * mm, v(-5.37, 38.25) * mm]});
            skFitSpline(sketch, "E724", {"points": [v(-5.37, 38.25) * mm, v(-5.37, 38.17) * mm, v(-5.42, 38.1) * mm, v(-5.47, 38.1) * mm]});
            skFitSpline(sketch, "E725", {"points": [v(-5.47, 38.1) * mm, v(-5.52, 38.1) * mm, v(-5.58, 38) * mm, v(-5.6, 37.86) * mm]});
            skFitSpline(sketch, "E726", {"points": [v(-5.6, 37.86) * mm, v(-5.63, 37.65) * mm, v(-5.7, 37.63) * mm, v(-6.34, 37.6) * mm]});
            skFitSpline(sketch, "E727", {"points": [v(17.54, 44.14) * mm, v(16.95, 44.77) * mm, v(17.5, 45.87) * mm, v(18.4, 45.87) * mm]});
            skFitSpline(sketch, "E728", {"points": [v(18.4, 45.87) * mm, v(18.98, 45.87) * mm, v(19.2, 45.64) * mm, v(19.2, 45.01) * mm]});
            skFitSpline(sketch, "E729", {"points": [v(19.2, 45.01) * mm, v(19.2, 44.08) * mm, v(18.12, 43.52) * mm, v(17.54, 44.14) * mm]});
            skLineSegment(sketch, "E730", {"start": v(-6.34, 37.6) * mm, "end": v(-7.05, 37.57) * mm});
            skLineSegment(sketch, "E731", {"start": v(-7.05, 37.57) * mm, "end": v(-7.05, 37.92) * mm});
            skLineSegment(sketch, "E732", {"start": v(-7.05, 37.92) * mm, "end": v(-6.34, 37.6) * mm});
            skCircle(sketch, "E733", {"center": v(0, 0) * mm, "radius": 34.93 * mm, "construction": true});
            skSolve(sketch);
        }
        {
            var Q0;
            Q0 = qSketchRegion(id + "F4", true);
            extrude(context, id + "F5", {"entities" : qUnion([Q0]), "operationType" : NewBodyOperationType.REMOVE, "oppositeDirection" : true, "depth" : 1.59 * mm});
        }
    });
